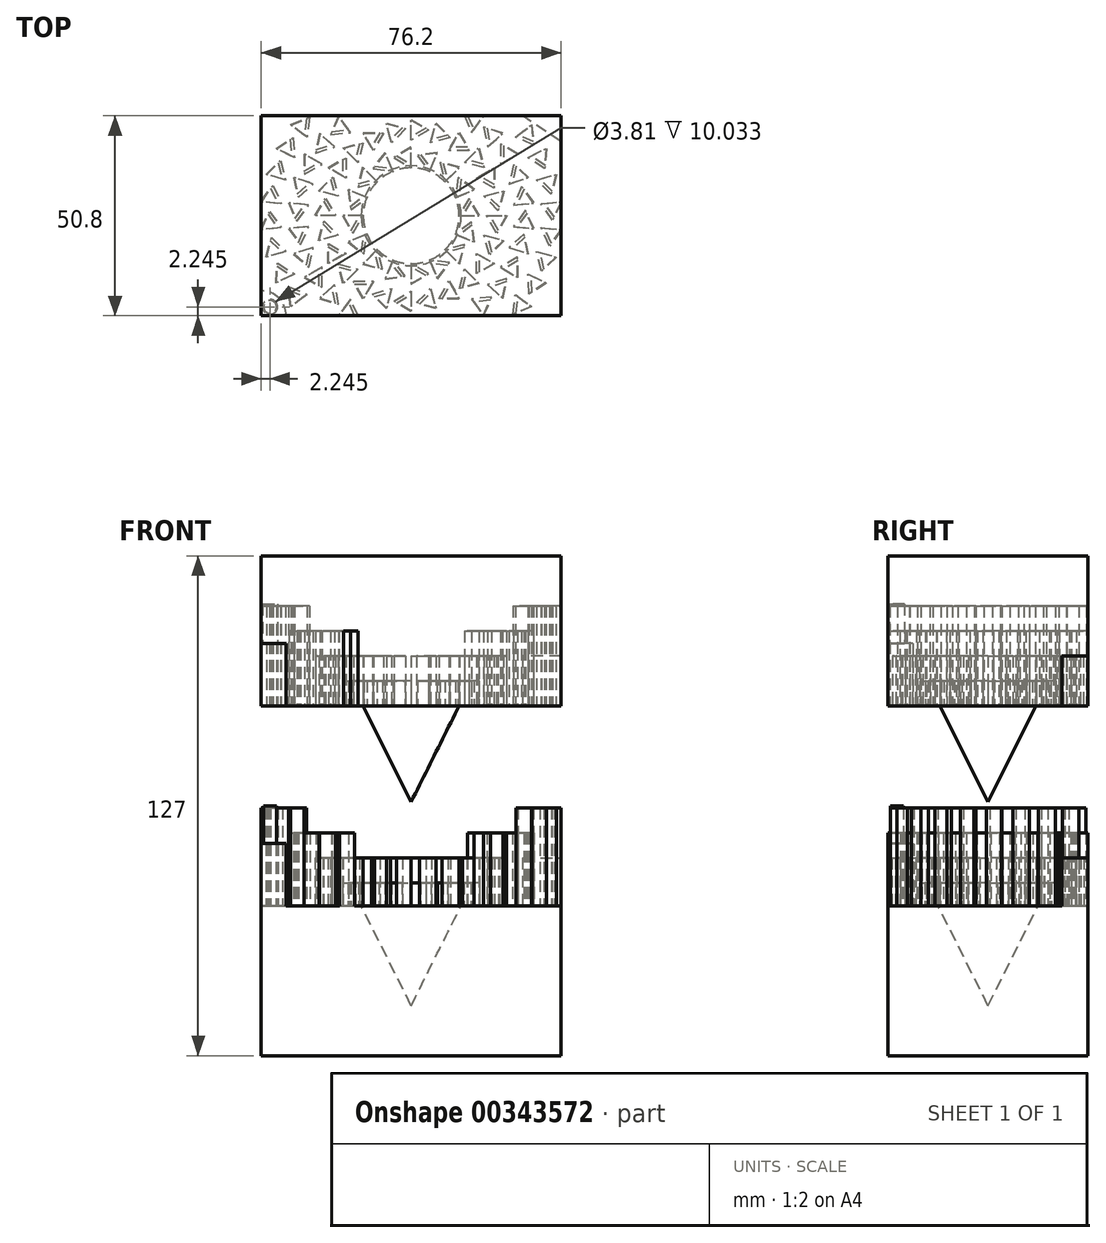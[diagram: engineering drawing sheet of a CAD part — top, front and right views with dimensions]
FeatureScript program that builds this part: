
annotation { "Feature Type Name" : "Feature", "Feature Type Description" : "" }
export const myFeature = defineFeature(function(context is Context, id is Id, definition is map)
    precondition{}
    {
        {
            var Q0;
            Q0=qCreatedBy(makeId("Top.planeOp"),FACE);
            var sketch = newSketch(context, id + "F0", { "sketchPlane" : qUnion([Q0])});
            skLineSegment(sketch, "E0.bottom", {"start": v(-38.1, 25.4) * mm, "end": v(38.1, 25.4) * mm});
            skLineSegment(sketch, "E0.top", {"start": v(-38.1, -25.4) * mm, "end": v(38.1, -25.4) * mm});
            skLineSegment(sketch, "E0.left", {"start": v(-38.1, 25.4) * mm, "end": v(-38.1, -25.4) * mm});
            skLineSegment(sketch, "E0.right", {"start": v(38.1, 25.4) * mm, "end": v(38.1, -25.4) * mm});
            skPoint(sketch, "E0.middle", {"position": v(0, 0) * mm});
            skSolve(sketch);
        }
        {
            var Q0;
            Q0=makeQuery(id+"F0.imprint","IMPRINT",FACE,{"disambiguationData":[TD([[makeQuery(id+"F0.imprint","IMPRINT",EDGE,{"derivedFrom":sQuery(id+"F0.wireOp",EDGE,"E0.bottom")}),-1.0]])]});
            extrude(context, id + "F1", {"entities" : qUnion([Q0]), "depth" : 38.1 * mm});
        }
        {
            var Q0;
            Q0=qCreatedBy(makeId("Top.planeOp"),FACE);
            cPlane(context, id + "F2", {"entities" : qUnion([Q0]), "cplaneType" : CPlaneType.OFFSET, "offset" : 127 * mm, "width" : 152.4 * mm, "height" : 152.4 * mm});
        }
        {
            var Q0;
            Q0=qCreatedBy(id+"F2.planeOp",FACE);
            var sketch = newSketch(context, id + "F3", { "sketchPlane" : qUnion([Q0])});
            skLineSegment(sketch, "E1.bottom", {"start": v(38.1, 25.4) * mm, "end": v(-38.1, 25.4) * mm});
            skLineSegment(sketch, "E1.top", {"start": v(38.1, -25.4) * mm, "end": v(-38.1, -25.4) * mm});
            skLineSegment(sketch, "E1.left", {"start": v(38.1, 25.4) * mm, "end": v(38.1, -25.4) * mm});
            skLineSegment(sketch, "E1.right", {"start": v(-38.1, 25.4) * mm, "end": v(-38.1, -25.4) * mm});
            skPoint(sketch, "E1.middle", {"position": v(0, 0) * mm});
            skSolve(sketch);
        }
        {
            var Q0;
            Q0=makeQuery(id+"F3.imprint","IMPRINT",FACE,{"disambiguationData":[TD([[makeQuery(id+"F3.imprint","IMPRINT",EDGE,{"derivedFrom":sQuery(id+"F3.wireOp",EDGE,"E1.bottom")}),1.0]])]});
            extrude(context, id + "F4", {"entities" : qUnion([Q0]), "oppositeDirection" : true, "depth" : 38.1 * mm});
        }
        {
            var Q0;
            Q0=makeQuery(id+"F4.opExtrude","CAP_FACE",FACE,{"disambiguationData":[OSD([sQuery(id+"F3.wireOp",EDGE,"E1.bottom"),sQuery(id+"F3.wireOp",EDGE,"E1.top"),sQuery(id+"F3.wireOp",EDGE,"E1.left"),sQuery(id+"F3.wireOp",EDGE,"E1.right")])],"isStart":false});
            var sketch = newSketch(context, id + "F5", { "sketchPlane" : qUnion([Q0])});
            skCircle(sketch, "E2", {"center": v(0, 0) * mm, "radius": 12.2 * mm});
            skSolve(sketch);
        }
        {
            var Q0;
            Q0=qCreatedBy(id+"F2.planeOp",FACE);
            cPlane(context, id + "F6", {"entities" : qUnion([Q0]), "cplaneType" : CPlaneType.OFFSET, "offset" : 62.48 * mm, "oppositeDirection" : true, "width" : 152.4 * mm, "height" : 152.4 * mm});
        }
        {
            var Q0;
            Q0=qCreatedBy(id+"F6.planeOp",FACE);
            var sketch = newSketch(context, id + "F7", { "sketchPlane" : qUnion([Q0])});
            skPoint(sketch, "E3", {"position": v(0, 0) * mm});
            skSolve(sketch);
        }
        {
            var Q1;
            Q1=makeQuery(id+"F5.imprint","IMPRINT",FACE,{"disambiguationData":[TD([[makeQuery(id+"F5.imprint","IMPRINT",EDGE,{"derivedFrom":sQuery(id+"F5.wireOp",EDGE,"E2")}),1.0]])]});
            var Q2;
            Q2=sQuery(id+"F7.wireOp",VERTEX,"E3");
            loft(context, id + "F8", {"operationType" : NewBodyOperationType.ADD, "sheetProfilesArray" : [{ "sheetProfileEntities" : qUnion([Q1]) }, { "sheetProfileEntities" : qUnion([Q2]) }]});
        }
        {
            var Q0;
            Q0=makeQuery(id+"F1.opExtrude","CAP_EDGE",EDGE,{"disambiguationData":[OSD([sQuery(id+"F0.wireOp",EDGE,"E0.bottom")])],"isStart":false});
            cPoint(context, id + "F9", {"entities" : qUnion([Q0]), "parameter" : 0.5});
        }
        {
            var Q0;
            Q0=makeQuery(id+"F1.opExtrude","CAP_EDGE",EDGE,{"disambiguationData":[OSD([sQuery(id+"F0.wireOp",EDGE,"E0.top")])],"isStart":false});
            cPoint(context, id + "F10", {"entities" : qUnion([Q0]), "parameter" : 0.5});
        }
        {
            var Q0;
            Q0=qCreatedBy(makeId("Origin.pointOp"),VERTEX);
            var Q1;
            Q1 = qCreatedBy(id + "F9" ,VERTEX);
            var Q2;
            Q2 = qCreatedBy(id + "F10" ,VERTEX);
            cPlane(context, id + "F11", {"entities" : qUnion([Q0, Q1, Q2]), "cplaneType" : CPlaneType.THREE_POINT, "offset" : 25.4 * mm, "width" : 152.4 * mm, "height" : 152.4 * mm});
        }
        {
            var Q0;
            Q0=makeQuery(id+"F4.opExtrude","CAP_FACE",FACE,{"disambiguationData":[OSD([sQuery(id+"F3.wireOp",EDGE,"E1.bottom"),sQuery(id+"F3.wireOp",EDGE,"E1.top"),sQuery(id+"F3.wireOp",EDGE,"E1.left"),sQuery(id+"F3.wireOp",EDGE,"E1.right")])],"isStart":false});
            var sketch = newSketch(context, id + "F12", { "sketchPlane" : qUnion([Q0])});
            skLineSegment(sketch, "E4", {"start": v(0, 12.2) * mm, "end": v(0, 17.27) * mm});
            skLineSegment(sketch, "E5", {"start": v(0, 17.27) * mm, "end": v(4.4, 14.73) * mm});
            skLineSegment(sketch, "E6", {"start": v(4.4, 14.73) * mm, "end": v(0, 12.2) * mm});
            skLineSegment(sketch, "E7.1.0", {"start": v(-6.6, 15.96) * mm, "end": v(-1.57, 15.3) * mm});
            skLineSegment(sketch, "E7.1.1", {"start": v(-1.57, 15.3) * mm, "end": v(-4.67, 11.26) * mm});
            skLineSegment(sketch, "E7.1.2", {"start": v(-4.67, 11.26) * mm, "end": v(-6.6, 15.96) * mm});
            skLineSegment(sketch, "E7.2.0", {"start": v(-12.21, 12.21) * mm, "end": v(-7.3, 13.53) * mm});
            skLineSegment(sketch, "E7.2.1", {"start": v(-7.3, 13.53) * mm, "end": v(-8.62, 8.62) * mm});
            skLineSegment(sketch, "E7.2.2", {"start": v(-8.62, 8.62) * mm, "end": v(-12.21, 12.21) * mm});
            skPoint(sketch, "E7.center", {"position": v(0, 0) * mm});
            skLineSegment(sketch, "E8.1.3.0", {"start": v(-15.96, 6.6) * mm, "end": v(-11.93, 9.7) * mm});
            skLineSegment(sketch, "E8.3.3.0", {"start": v(-11.93, 9.7) * mm, "end": v(-11.26, 4.67) * mm});
            skLineSegment(sketch, "E8.6.3.0", {"start": v(-11.26, 4.67) * mm, "end": v(-15.96, 6.6) * mm});
            skLineSegment(sketch, "E8.1.4.0", {"start": v(-17.27, 0) * mm, "end": v(-14.73, 4.4) * mm});
            skLineSegment(sketch, "E8.3.4.0", {"start": v(-14.73, 4.4) * mm, "end": v(-12.2, 0) * mm});
            skLineSegment(sketch, "E8.6.4.0", {"start": v(-12.2, 0) * mm, "end": v(-17.27, 0) * mm});
            skLineSegment(sketch, "E8.1.5.0", {"start": v(-15.96, -6.6) * mm, "end": v(-15.3, -1.57) * mm});
            skLineSegment(sketch, "E8.3.5.0", {"start": v(-15.3, -1.57) * mm, "end": v(-11.26, -4.67) * mm});
            skLineSegment(sketch, "E8.6.5.0", {"start": v(-11.26, -4.67) * mm, "end": v(-15.96, -6.6) * mm});
            skLineSegment(sketch, "E8.1.6.0", {"start": v(-12.21, -12.21) * mm, "end": v(-13.53, -7.3) * mm});
            skLineSegment(sketch, "E8.3.6.0", {"start": v(-13.53, -7.3) * mm, "end": v(-8.62, -8.62) * mm});
            skLineSegment(sketch, "E8.6.6.0", {"start": v(-8.62, -8.62) * mm, "end": v(-12.21, -12.21) * mm});
            skLineSegment(sketch, "E8.1.7.0", {"start": v(-6.6, -15.96) * mm, "end": v(-9.7, -11.93) * mm});
            skLineSegment(sketch, "E8.3.7.0", {"start": v(-9.7, -11.93) * mm, "end": v(-4.67, -11.26) * mm});
            skLineSegment(sketch, "E8.6.7.0", {"start": v(-4.67, -11.26) * mm, "end": v(-6.6, -15.96) * mm});
            skLineSegment(sketch, "E9.1.8.0", {"start": v(0, -17.27) * mm, "end": v(-4.4, -14.73) * mm});
            skLineSegment(sketch, "E9.3.8.0", {"start": v(-4.4, -14.73) * mm, "end": v(0, -12.2) * mm});
            skLineSegment(sketch, "E9.6.8.0", {"start": v(0, -12.2) * mm, "end": v(0, -17.27) * mm});
            skLineSegment(sketch, "E10.1.9.0", {"start": v(6.6, -15.96) * mm, "end": v(1.57, -15.3) * mm});
            skLineSegment(sketch, "E10.3.9.0", {"start": v(1.57, -15.3) * mm, "end": v(4.67, -11.26) * mm});
            skLineSegment(sketch, "E10.6.9.0", {"start": v(4.67, -11.26) * mm, "end": v(6.6, -15.96) * mm});
            skLineSegment(sketch, "E10.1.10.0", {"start": v(12.21, -12.21) * mm, "end": v(7.3, -13.53) * mm});
            skLineSegment(sketch, "E10.3.10.0", {"start": v(7.3, -13.53) * mm, "end": v(8.62, -8.62) * mm});
            skLineSegment(sketch, "E10.6.10.0", {"start": v(8.62, -8.62) * mm, "end": v(12.21, -12.21) * mm});
            skLineSegment(sketch, "E11.1.11.0", {"start": v(15.96, -6.6) * mm, "end": v(11.93, -9.7) * mm});
            skLineSegment(sketch, "E11.3.11.0", {"start": v(11.93, -9.7) * mm, "end": v(11.26, -4.67) * mm});
            skLineSegment(sketch, "E11.6.11.0", {"start": v(11.26, -4.67) * mm, "end": v(15.96, -6.6) * mm});
            skLineSegment(sketch, "E12.1.12.0", {"start": v(17.27, 0) * mm, "end": v(14.73, -4.4) * mm});
            skLineSegment(sketch, "E12.3.12.0", {"start": v(14.73, -4.4) * mm, "end": v(12.2, 0) * mm});
            skLineSegment(sketch, "E12.6.12.0", {"start": v(12.2, 0) * mm, "end": v(17.27, 0) * mm});
            skLineSegment(sketch, "E12.1.13.0", {"start": v(15.96, 6.6) * mm, "end": v(15.3, 1.57) * mm});
            skLineSegment(sketch, "E12.3.13.0", {"start": v(15.3, 1.57) * mm, "end": v(11.26, 4.67) * mm});
            skLineSegment(sketch, "E12.6.13.0", {"start": v(11.26, 4.67) * mm, "end": v(15.96, 6.6) * mm});
            skLineSegment(sketch, "E12.1.14.0", {"start": v(12.21, 12.21) * mm, "end": v(13.53, 7.3) * mm});
            skLineSegment(sketch, "E12.3.14.0", {"start": v(13.53, 7.3) * mm, "end": v(8.62, 8.62) * mm});
            skLineSegment(sketch, "E12.6.14.0", {"start": v(8.62, 8.62) * mm, "end": v(12.21, 12.21) * mm});
            skLineSegment(sketch, "E12.1.15.0", {"start": v(6.6, 15.96) * mm, "end": v(9.7, 11.93) * mm});
            skLineSegment(sketch, "E12.3.15.0", {"start": v(9.7, 11.93) * mm, "end": v(4.67, 11.26) * mm});
            skLineSegment(sketch, "E12.6.15.0", {"start": v(4.67, 11.26) * mm, "end": v(6.6, 15.96) * mm});
            skLineSegment(sketch, "E13", {"start": v(0, 19.18) * mm, "end": v(0, 24.26) * mm});
            skLineSegment(sketch, "E14", {"start": v(0, 24.26) * mm, "end": v(-4.4, 21.72) * mm});
            skLineSegment(sketch, "E15", {"start": v(-4.4, 21.72) * mm, "end": v(0, 19.18) * mm});
            skLineSegment(sketch, "E16.1.0", {"start": v(-6.28, 23.43) * mm, "end": v(-9.87, 19.84) * mm});
            skLineSegment(sketch, "E16.1.1", {"start": v(-4.96, 18.52) * mm, "end": v(-6.28, 23.43) * mm});
            skLineSegment(sketch, "E16.1.2", {"start": v(-9.87, 19.84) * mm, "end": v(-4.96, 18.52) * mm});
            skLineSegment(sketch, "E16.2.0", {"start": v(-12.13, 21) * mm, "end": v(-14.67, 16.6) * mm});
            skLineSegment(sketch, "E16.2.1", {"start": v(-9.59, 16.6) * mm, "end": v(-12.13, 21) * mm});
            skLineSegment(sketch, "E16.2.2", {"start": v(-14.67, 16.6) * mm, "end": v(-9.59, 16.6) * mm});
            skLineSegment(sketch, "E17.2.3.0", {"start": v(-17.15, 17.15) * mm, "end": v(-18.47, 12.25) * mm});
            skLineSegment(sketch, "E17.3.3.0", {"start": v(-13.56, 13.56) * mm, "end": v(-17.15, 17.15) * mm});
            skLineSegment(sketch, "E17.6.3.0", {"start": v(-18.47, 12.25) * mm, "end": v(-13.56, 13.56) * mm});
            skLineSegment(sketch, "E17.2.4.0", {"start": v(-21, 12.13) * mm, "end": v(-21, 7.05) * mm});
            skLineSegment(sketch, "E17.3.4.0", {"start": v(-16.6, 9.59) * mm, "end": v(-21, 12.13) * mm});
            skLineSegment(sketch, "E17.6.4.0", {"start": v(-21, 7.05) * mm, "end": v(-16.6, 9.59) * mm});
            skLineSegment(sketch, "E17.2.5.0", {"start": v(-23.43, 6.28) * mm, "end": v(-22.12, 1.37) * mm});
            skLineSegment(sketch, "E17.3.5.0", {"start": v(-18.52, 4.96) * mm, "end": v(-23.43, 6.28) * mm});
            skLineSegment(sketch, "E17.6.5.0", {"start": v(-22.12, 1.37) * mm, "end": v(-18.52, 4.96) * mm});
            skLineSegment(sketch, "E17.2.6.0", {"start": v(-24.26, 0) * mm, "end": v(-21.72, -4.4) * mm});
            skLineSegment(sketch, "E17.3.6.0", {"start": v(-19.18, 0) * mm, "end": v(-24.26, 0) * mm});
            skLineSegment(sketch, "E17.6.6.0", {"start": v(-21.72, -4.4) * mm, "end": v(-19.18, 0) * mm});
            skLineSegment(sketch, "E17.2.7.0", {"start": v(-23.43, -6.28) * mm, "end": v(-19.84, -9.87) * mm});
            skLineSegment(sketch, "E17.3.7.0", {"start": v(-18.52, -4.96) * mm, "end": v(-23.43, -6.28) * mm});
            skLineSegment(sketch, "E17.6.7.0", {"start": v(-19.84, -9.87) * mm, "end": v(-18.52, -4.96) * mm});
            skLineSegment(sketch, "E17.2.8.0", {"start": v(-21, -12.13) * mm, "end": v(-16.6, -14.67) * mm});
            skLineSegment(sketch, "E17.3.8.0", {"start": v(-16.6, -9.59) * mm, "end": v(-21, -12.13) * mm});
            skLineSegment(sketch, "E17.6.8.0", {"start": v(-16.6, -14.67) * mm, "end": v(-16.6, -9.59) * mm});
            skLineSegment(sketch, "E17.2.9.0", {"start": v(-17.15, -17.15) * mm, "end": v(-12.25, -18.47) * mm});
            skLineSegment(sketch, "E17.3.9.0", {"start": v(-13.56, -13.56) * mm, "end": v(-17.15, -17.15) * mm});
            skLineSegment(sketch, "E17.6.9.0", {"start": v(-12.25, -18.47) * mm, "end": v(-13.56, -13.56) * mm});
            skLineSegment(sketch, "E17.2.10.0", {"start": v(-12.13, -21) * mm, "end": v(-7.05, -21) * mm});
            skLineSegment(sketch, "E17.3.10.0", {"start": v(-9.59, -16.6) * mm, "end": v(-12.13, -21) * mm});
            skLineSegment(sketch, "E17.6.10.0", {"start": v(-7.05, -21) * mm, "end": v(-9.59, -16.6) * mm});
            skLineSegment(sketch, "E17.2.11.0", {"start": v(-6.28, -23.43) * mm, "end": v(-1.37, -22.12) * mm});
            skLineSegment(sketch, "E17.3.11.0", {"start": v(-4.96, -18.52) * mm, "end": v(-6.28, -23.43) * mm});
            skLineSegment(sketch, "E17.6.11.0", {"start": v(-1.37, -22.12) * mm, "end": v(-4.96, -18.52) * mm});
            skLineSegment(sketch, "E17.2.12.0", {"start": v(0, -24.26) * mm, "end": v(4.4, -21.72) * mm});
            skLineSegment(sketch, "E17.3.12.0", {"start": v(0, -19.18) * mm, "end": v(0, -24.26) * mm});
            skLineSegment(sketch, "E17.6.12.0", {"start": v(4.4, -21.72) * mm, "end": v(0, -19.18) * mm});
            skLineSegment(sketch, "E17.2.13.0", {"start": v(6.28, -23.43) * mm, "end": v(9.87, -19.84) * mm});
            skLineSegment(sketch, "E17.3.13.0", {"start": v(4.96, -18.52) * mm, "end": v(6.28, -23.43) * mm});
            skLineSegment(sketch, "E17.6.13.0", {"start": v(9.87, -19.84) * mm, "end": v(4.96, -18.52) * mm});
            skLineSegment(sketch, "E17.2.14.0", {"start": v(12.13, -21) * mm, "end": v(14.67, -16.6) * mm});
            skLineSegment(sketch, "E17.3.14.0", {"start": v(9.59, -16.6) * mm, "end": v(12.13, -21) * mm});
            skLineSegment(sketch, "E17.6.14.0", {"start": v(14.67, -16.6) * mm, "end": v(9.59, -16.6) * mm});
            skLineSegment(sketch, "E17.2.15.0", {"start": v(17.15, -17.15) * mm, "end": v(18.47, -12.25) * mm});
            skLineSegment(sketch, "E17.3.15.0", {"start": v(13.56, -13.56) * mm, "end": v(17.15, -17.15) * mm});
            skLineSegment(sketch, "E17.6.15.0", {"start": v(18.47, -12.25) * mm, "end": v(13.56, -13.56) * mm});
            skLineSegment(sketch, "E17.2.16.0", {"start": v(21, -12.13) * mm, "end": v(21, -7.05) * mm});
            skLineSegment(sketch, "E17.3.16.0", {"start": v(16.6, -9.59) * mm, "end": v(21, -12.13) * mm});
            skLineSegment(sketch, "E17.6.16.0", {"start": v(21, -7.05) * mm, "end": v(16.6, -9.59) * mm});
            skLineSegment(sketch, "E17.2.17.0", {"start": v(23.43, -6.28) * mm, "end": v(22.12, -1.37) * mm});
            skLineSegment(sketch, "E17.3.17.0", {"start": v(18.52, -4.96) * mm, "end": v(23.43, -6.28) * mm});
            skLineSegment(sketch, "E17.6.17.0", {"start": v(22.12, -1.37) * mm, "end": v(18.52, -4.96) * mm});
            skLineSegment(sketch, "E17.2.18.0", {"start": v(24.26, 0) * mm, "end": v(21.72, 4.4) * mm});
            skLineSegment(sketch, "E17.3.18.0", {"start": v(19.18, 0) * mm, "end": v(24.26, 0) * mm});
            skLineSegment(sketch, "E17.6.18.0", {"start": v(21.72, 4.4) * mm, "end": v(19.18, 0) * mm});
            skLineSegment(sketch, "E17.2.19.0", {"start": v(23.43, 6.28) * mm, "end": v(19.84, 9.87) * mm});
            skLineSegment(sketch, "E17.3.19.0", {"start": v(18.52, 4.96) * mm, "end": v(23.43, 6.28) * mm});
            skLineSegment(sketch, "E17.6.19.0", {"start": v(19.84, 9.87) * mm, "end": v(18.52, 4.96) * mm});
            skLineSegment(sketch, "E17.2.20.0", {"start": v(21, 12.13) * mm, "end": v(16.6, 14.67) * mm});
            skLineSegment(sketch, "E17.3.20.0", {"start": v(16.6, 9.59) * mm, "end": v(21, 12.13) * mm});
            skLineSegment(sketch, "E17.6.20.0", {"start": v(16.6, 14.67) * mm, "end": v(16.6, 9.59) * mm});
            skLineSegment(sketch, "E17.2.21.0", {"start": v(17.15, 17.15) * mm, "end": v(12.25, 18.47) * mm});
            skLineSegment(sketch, "E17.3.21.0", {"start": v(13.56, 13.56) * mm, "end": v(17.15, 17.15) * mm});
            skLineSegment(sketch, "E17.6.21.0", {"start": v(12.25, 18.47) * mm, "end": v(13.56, 13.56) * mm});
            skLineSegment(sketch, "E17.2.22.0", {"start": v(12.13, 21) * mm, "end": v(7.05, 21) * mm});
            skLineSegment(sketch, "E17.3.22.0", {"start": v(9.59, 16.6) * mm, "end": v(12.13, 21) * mm});
            skLineSegment(sketch, "E17.6.22.0", {"start": v(7.05, 21) * mm, "end": v(9.59, 16.6) * mm});
            skLineSegment(sketch, "E17.2.23.0", {"start": v(6.28, 23.43) * mm, "end": v(1.37, 22.12) * mm});
            skLineSegment(sketch, "E17.3.23.0", {"start": v(4.96, 18.52) * mm, "end": v(6.28, 23.43) * mm});
            skLineSegment(sketch, "E17.6.23.0", {"start": v(1.37, 22.12) * mm, "end": v(4.96, 18.52) * mm});
            skLineSegment(sketch, "E18", {"start": v(0, 26.16) * mm, "end": v(0, 31.24) * mm});
            skPoint(sketch, "E18.startSnap0", {"position": v(0, 25.4) * mm});
            skLineSegment(sketch, "E19", {"start": v(0, 31.24) * mm, "end": v(4.4, 28.7) * mm});
            skLineSegment(sketch, "E20", {"start": v(4.4, 28.7) * mm, "end": v(0, 26.16) * mm});
            skLineSegment(sketch, "E21.1.0", {"start": v(-5.44, 25.6) * mm, "end": v(-6.5, 30.56) * mm});
            skLineSegment(sketch, "E21.1.1", {"start": v(-6.5, 30.56) * mm, "end": v(-1.66, 28.99) * mm});
            skLineSegment(sketch, "E21.1.2", {"start": v(-1.66, 28.99) * mm, "end": v(-5.44, 25.6) * mm});
            skLineSegment(sketch, "E21.2.0", {"start": v(-10.64, 23.9) * mm, "end": v(-12.7, 28.54) * mm});
            skLineSegment(sketch, "E21.2.1", {"start": v(-12.7, 28.54) * mm, "end": v(-7.66, 28) * mm});
            skLineSegment(sketch, "E21.2.2", {"start": v(-7.66, 28) * mm, "end": v(-10.64, 23.9) * mm});
            skLineSegment(sketch, "E22.1.3.0", {"start": v(-15.38, 21.17) * mm, "end": v(-18.36, 25.28) * mm});
            skLineSegment(sketch, "E22.3.3.0", {"start": v(-18.36, 25.28) * mm, "end": v(-13.31, 25.8) * mm});
            skLineSegment(sketch, "E22.6.3.0", {"start": v(-13.31, 25.8) * mm, "end": v(-15.38, 21.17) * mm});
            skLineSegment(sketch, "E22.1.4.0", {"start": v(-19.44, 17.5) * mm, "end": v(-23.22, 20.9) * mm});
            skLineSegment(sketch, "E22.3.4.0", {"start": v(-23.22, 20.9) * mm, "end": v(-18.39, 22.47) * mm});
            skLineSegment(sketch, "E22.6.4.0", {"start": v(-18.39, 22.47) * mm, "end": v(-19.44, 17.5) * mm});
            skLineSegment(sketch, "E22.1.5.0", {"start": v(-22.66, 13.08) * mm, "end": v(-27.06, 15.62) * mm});
            skLineSegment(sketch, "E22.3.5.0", {"start": v(-27.06, 15.62) * mm, "end": v(-22.66, 18.16) * mm});
            skLineSegment(sketch, "E22.6.5.0", {"start": v(-22.66, 18.16) * mm, "end": v(-22.66, 13.08) * mm});
            skLineSegment(sketch, "E22.1.6.0", {"start": v(-24.88, 8.08) * mm, "end": v(-29.71, 9.65) * mm});
            skLineSegment(sketch, "E22.3.6.0", {"start": v(-29.71, 9.65) * mm, "end": v(-25.94, 13.05) * mm});
            skLineSegment(sketch, "E22.6.6.0", {"start": v(-25.94, 13.05) * mm, "end": v(-24.88, 8.08) * mm});
            skLineSegment(sketch, "E22.1.7.0", {"start": v(-26.02, 2.73) * mm, "end": v(-31.07, 3.27) * mm});
            skLineSegment(sketch, "E22.3.7.0", {"start": v(-31.07, 3.27) * mm, "end": v(-28.08, 7.38) * mm});
            skLineSegment(sketch, "E22.6.7.0", {"start": v(-28.08, 7.38) * mm, "end": v(-26.02, 2.73) * mm});
            skLineSegment(sketch, "E22.1.8.0", {"start": v(-26.02, -2.73) * mm, "end": v(-31.07, -3.27) * mm});
            skLineSegment(sketch, "E22.3.8.0", {"start": v(-31.07, -3.27) * mm, "end": v(-29, 1.38) * mm});
            skLineSegment(sketch, "E22.6.8.0", {"start": v(-29, 1.38) * mm, "end": v(-26.02, -2.73) * mm});
            skLineSegment(sketch, "E22.1.9.0", {"start": v(-24.88, -8.08) * mm, "end": v(-29.71, -9.65) * mm});
            skLineSegment(sketch, "E22.3.9.0", {"start": v(-29.71, -9.65) * mm, "end": v(-28.66, -4.69) * mm});
            skLineSegment(sketch, "E22.6.9.0", {"start": v(-28.66, -4.69) * mm, "end": v(-24.88, -8.08) * mm});
            skLineSegment(sketch, "E22.1.10.0", {"start": v(-22.66, -13.08) * mm, "end": v(-27.06, -15.62) * mm});
            skLineSegment(sketch, "E22.3.10.0", {"start": v(-27.06, -15.62) * mm, "end": v(-27.06, -10.54) * mm});
            skLineSegment(sketch, "E22.6.10.0", {"start": v(-27.06, -10.54) * mm, "end": v(-22.66, -13.08) * mm});
            skLineSegment(sketch, "E22.1.11.0", {"start": v(-19.44, -17.5) * mm, "end": v(-23.22, -20.9) * mm});
            skLineSegment(sketch, "E22.3.11.0", {"start": v(-23.22, -20.9) * mm, "end": v(-24.27, -15.94) * mm});
            skLineSegment(sketch, "E22.6.11.0", {"start": v(-24.27, -15.94) * mm, "end": v(-19.44, -17.5) * mm});
            skLineSegment(sketch, "E22.1.12.0", {"start": v(-15.38, -21.17) * mm, "end": v(-18.36, -25.28) * mm});
            skLineSegment(sketch, "E22.3.12.0", {"start": v(-18.36, -25.28) * mm, "end": v(-20.43, -20.63) * mm});
            skLineSegment(sketch, "E22.6.12.0", {"start": v(-20.43, -20.63) * mm, "end": v(-15.38, -21.17) * mm});
            skLineSegment(sketch, "E22.1.13.0", {"start": v(-10.64, -23.9) * mm, "end": v(-12.7, -28.54) * mm});
            skLineSegment(sketch, "E22.3.13.0", {"start": v(-12.7, -28.54) * mm, "end": v(-15.7, -24.43) * mm});
            skLineSegment(sketch, "E22.6.13.0", {"start": v(-15.7, -24.43) * mm, "end": v(-10.64, -23.9) * mm});
            skLineSegment(sketch, "E22.1.14.0", {"start": v(-5.44, -25.6) * mm, "end": v(-6.5, -30.56) * mm});
            skLineSegment(sketch, "E22.3.14.0", {"start": v(-6.5, -30.56) * mm, "end": v(-10.27, -27.16) * mm});
            skLineSegment(sketch, "E22.6.14.0", {"start": v(-10.27, -27.16) * mm, "end": v(-5.44, -25.6) * mm});
            skLineSegment(sketch, "E22.1.15.0", {"start": v(0, -26.16) * mm, "end": v(0, -31.24) * mm});
            skLineSegment(sketch, "E22.3.15.0", {"start": v(0, -31.24) * mm, "end": v(-4.4, -28.7) * mm});
            skLineSegment(sketch, "E22.6.15.0", {"start": v(-4.4, -28.7) * mm, "end": v(0, -26.16) * mm});
            skLineSegment(sketch, "E22.1.16.0", {"start": v(5.44, -25.6) * mm, "end": v(6.5, -30.56) * mm});
            skLineSegment(sketch, "E22.3.16.0", {"start": v(6.5, -30.56) * mm, "end": v(1.66, -28.99) * mm});
            skLineSegment(sketch, "E22.6.16.0", {"start": v(1.66, -28.99) * mm, "end": v(5.44, -25.6) * mm});
            skLineSegment(sketch, "E22.1.17.0", {"start": v(10.64, -23.9) * mm, "end": v(12.7, -28.54) * mm});
            skLineSegment(sketch, "E22.3.17.0", {"start": v(12.7, -28.54) * mm, "end": v(7.66, -28) * mm});
            skLineSegment(sketch, "E22.6.17.0", {"start": v(7.66, -28) * mm, "end": v(10.64, -23.9) * mm});
            skLineSegment(sketch, "E22.1.18.0", {"start": v(15.38, -21.17) * mm, "end": v(18.36, -25.28) * mm});
            skLineSegment(sketch, "E22.3.18.0", {"start": v(18.36, -25.28) * mm, "end": v(13.31, -25.8) * mm});
            skLineSegment(sketch, "E22.6.18.0", {"start": v(13.31, -25.8) * mm, "end": v(15.38, -21.17) * mm});
            skLineSegment(sketch, "E22.1.19.0", {"start": v(19.44, -17.5) * mm, "end": v(23.22, -20.9) * mm});
            skLineSegment(sketch, "E22.3.19.0", {"start": v(23.22, -20.9) * mm, "end": v(18.39, -22.47) * mm});
            skLineSegment(sketch, "E22.6.19.0", {"start": v(18.39, -22.47) * mm, "end": v(19.44, -17.5) * mm});
            skLineSegment(sketch, "E22.1.20.0", {"start": v(22.66, -13.08) * mm, "end": v(27.06, -15.62) * mm});
            skLineSegment(sketch, "E22.3.20.0", {"start": v(27.06, -15.62) * mm, "end": v(22.66, -18.16) * mm});
            skLineSegment(sketch, "E22.6.20.0", {"start": v(22.66, -18.16) * mm, "end": v(22.66, -13.08) * mm});
            skLineSegment(sketch, "E22.1.21.0", {"start": v(24.88, -8.08) * mm, "end": v(29.71, -9.65) * mm});
            skLineSegment(sketch, "E22.3.21.0", {"start": v(29.71, -9.65) * mm, "end": v(25.94, -13.05) * mm});
            skLineSegment(sketch, "E22.6.21.0", {"start": v(25.94, -13.05) * mm, "end": v(24.88, -8.08) * mm});
            skLineSegment(sketch, "E22.1.22.0", {"start": v(26.02, -2.73) * mm, "end": v(31.07, -3.27) * mm});
            skLineSegment(sketch, "E22.3.22.0", {"start": v(31.07, -3.27) * mm, "end": v(28.08, -7.38) * mm});
            skLineSegment(sketch, "E22.6.22.0", {"start": v(28.08, -7.38) * mm, "end": v(26.02, -2.73) * mm});
            skLineSegment(sketch, "E22.1.23.0", {"start": v(26.02, 2.73) * mm, "end": v(31.07, 3.27) * mm});
            skLineSegment(sketch, "E22.3.23.0", {"start": v(31.07, 3.27) * mm, "end": v(29, -1.38) * mm});
            skLineSegment(sketch, "E22.6.23.0", {"start": v(29, -1.38) * mm, "end": v(26.02, 2.73) * mm});
            skLineSegment(sketch, "E22.1.24.0", {"start": v(24.88, 8.08) * mm, "end": v(29.71, 9.65) * mm});
            skLineSegment(sketch, "E22.3.24.0", {"start": v(29.71, 9.65) * mm, "end": v(28.66, 4.69) * mm});
            skLineSegment(sketch, "E22.6.24.0", {"start": v(28.66, 4.69) * mm, "end": v(24.88, 8.08) * mm});
            skLineSegment(sketch, "E22.1.25.0", {"start": v(22.66, 13.08) * mm, "end": v(27.06, 15.62) * mm});
            skLineSegment(sketch, "E22.3.25.0", {"start": v(27.06, 15.62) * mm, "end": v(27.06, 10.54) * mm});
            skLineSegment(sketch, "E22.6.25.0", {"start": v(27.06, 10.54) * mm, "end": v(22.66, 13.08) * mm});
            skLineSegment(sketch, "E22.1.26.0", {"start": v(19.44, 17.5) * mm, "end": v(23.22, 20.9) * mm});
            skLineSegment(sketch, "E22.3.26.0", {"start": v(23.22, 20.9) * mm, "end": v(24.27, 15.94) * mm});
            skLineSegment(sketch, "E22.6.26.0", {"start": v(24.27, 15.94) * mm, "end": v(19.44, 17.5) * mm});
            skLineSegment(sketch, "E22.1.27.0", {"start": v(15.38, 21.17) * mm, "end": v(18.36, 25.28) * mm});
            skLineSegment(sketch, "E22.3.27.0", {"start": v(18.36, 25.28) * mm, "end": v(20.43, 20.63) * mm});
            skLineSegment(sketch, "E22.6.27.0", {"start": v(20.43, 20.63) * mm, "end": v(15.38, 21.17) * mm});
            skLineSegment(sketch, "E22.1.28.0", {"start": v(10.64, 23.9) * mm, "end": v(12.7, 28.54) * mm});
            skLineSegment(sketch, "E22.3.28.0", {"start": v(12.7, 28.54) * mm, "end": v(15.7, 24.43) * mm});
            skLineSegment(sketch, "E22.6.28.0", {"start": v(15.7, 24.43) * mm, "end": v(10.64, 23.9) * mm});
            skLineSegment(sketch, "E22.1.29.0", {"start": v(5.44, 25.6) * mm, "end": v(6.5, 30.56) * mm});
            skLineSegment(sketch, "E22.3.29.0", {"start": v(6.5, 30.56) * mm, "end": v(10.27, 27.16) * mm});
            skLineSegment(sketch, "E22.6.29.0", {"start": v(10.27, 27.16) * mm, "end": v(5.44, 25.6) * mm});
            skLineSegment(sketch, "E23", {"start": v(0, 33.15) * mm, "end": v(0, 38.23) * mm});
            skLineSegment(sketch, "E24", {"start": v(0, 38.23) * mm, "end": v(-4.4, 35.69) * mm});
            skLineSegment(sketch, "E25", {"start": v(-4.4, 35.69) * mm, "end": v(0, 33.15) * mm});
            skLineSegment(sketch, "E26.1.0", {"start": v(-6.1, 32.58) * mm, "end": v(-7.02, 37.58) * mm});
            skLineSegment(sketch, "E26.1.1", {"start": v(-7.02, 37.58) * mm, "end": v(-10.88, 34.27) * mm});
            skLineSegment(sketch, "E26.1.2", {"start": v(-10.88, 34.27) * mm, "end": v(-6.1, 32.58) * mm});
            skLineSegment(sketch, "E26.2.0", {"start": v(-11.97, 30.9) * mm, "end": v(-13.8, 35.65) * mm});
            skLineSegment(sketch, "E26.2.1", {"start": v(-13.8, 35.65) * mm, "end": v(-17, 31.69) * mm});
            skLineSegment(sketch, "E26.2.2", {"start": v(-17, 31.69) * mm, "end": v(-11.97, 30.9) * mm});
            skLineSegment(sketch, "E27.1.3.0", {"start": v(-17.45, 28.18) * mm, "end": v(-20.12, 32.5) * mm});
            skLineSegment(sketch, "E27.3.3.0", {"start": v(-20.12, 32.5) * mm, "end": v(-22.53, 28.03) * mm});
            skLineSegment(sketch, "E27.6.3.0", {"start": v(-22.53, 28.03) * mm, "end": v(-17.45, 28.18) * mm});
            skLineSegment(sketch, "E27.1.4.0", {"start": v(-22.33, 24.5) * mm, "end": v(-25.75, 28.25) * mm});
            skLineSegment(sketch, "E27.3.4.0", {"start": v(-25.75, 28.25) * mm, "end": v(-27.3, 23.4) * mm});
            skLineSegment(sketch, "E27.6.4.0", {"start": v(-27.3, 23.4) * mm, "end": v(-22.33, 24.5) * mm});
            skLineSegment(sketch, "E27.1.5.0", {"start": v(-26.45, 19.98) * mm, "end": v(-30.5, 23.04) * mm});
            skLineSegment(sketch, "E27.3.5.0", {"start": v(-30.5, 23.04) * mm, "end": v(-31.13, 18) * mm});
            skLineSegment(sketch, "E27.6.5.0", {"start": v(-31.13, 18) * mm, "end": v(-26.45, 19.98) * mm});
            skLineSegment(sketch, "E27.1.6.0", {"start": v(-29.67, 14.77) * mm, "end": v(-34.22, 17.04) * mm});
            skLineSegment(sketch, "E27.3.6.0", {"start": v(-34.22, 17.04) * mm, "end": v(-33.9, 11.97) * mm});
            skLineSegment(sketch, "E27.6.6.0", {"start": v(-33.9, 11.97) * mm, "end": v(-29.67, 14.77) * mm});
            skLineSegment(sketch, "E27.1.7.0", {"start": v(-31.88, 9.07) * mm, "end": v(-36.77, 10.46) * mm});
            skLineSegment(sketch, "E27.3.7.0", {"start": v(-36.77, 10.46) * mm, "end": v(-35.53, 5.53) * mm});
            skLineSegment(sketch, "E27.6.7.0", {"start": v(-35.53, 5.53) * mm, "end": v(-31.88, 9.07) * mm});
            skLineSegment(sketch, "E27.1.8.0", {"start": v(-33, 3.06) * mm, "end": v(-38.06, 3.53) * mm});
            skLineSegment(sketch, "E27.3.8.0", {"start": v(-38.06, 3.53) * mm, "end": v(-35.94, -1.09) * mm});
            skLineSegment(sketch, "E27.6.8.0", {"start": v(-35.94, -1.09) * mm, "end": v(-33, 3.06) * mm});
            skLineSegment(sketch, "E27.1.9.0", {"start": v(-33, -3.06) * mm, "end": v(-38.06, -3.53) * mm});
            skLineSegment(sketch, "E27.3.9.0", {"start": v(-38.06, -3.53) * mm, "end": v(-35.13, -7.67) * mm});
            skLineSegment(sketch, "E27.6.9.0", {"start": v(-35.13, -7.67) * mm, "end": v(-33, -3.06) * mm});
            skLineSegment(sketch, "E27.1.10.0", {"start": v(-31.88, -9.07) * mm, "end": v(-36.77, -10.46) * mm});
            skLineSegment(sketch, "E27.3.10.0", {"start": v(-36.77, -10.46) * mm, "end": v(-33.12, -14) * mm});
            skLineSegment(sketch, "E27.6.10.0", {"start": v(-33.12, -14) * mm, "end": v(-31.88, -9.07) * mm});
            skLineSegment(sketch, "E27.1.11.0", {"start": v(-29.67, -14.77) * mm, "end": v(-34.22, -17.04) * mm});
            skLineSegment(sketch, "E27.3.11.0", {"start": v(-34.22, -17.04) * mm, "end": v(-29.98, -19.85) * mm});
            skLineSegment(sketch, "E27.6.11.0", {"start": v(-29.98, -19.85) * mm, "end": v(-29.67, -14.77) * mm});
            skLineSegment(sketch, "E27.1.12.0", {"start": v(-26.45, -19.98) * mm, "end": v(-30.5, -23.04) * mm});
            skLineSegment(sketch, "E27.3.12.0", {"start": v(-30.5, -23.04) * mm, "end": v(-25.83, -25.02) * mm});
            skLineSegment(sketch, "E27.6.12.0", {"start": v(-25.83, -25.02) * mm, "end": v(-26.45, -19.98) * mm});
            skLineSegment(sketch, "E27.1.13.0", {"start": v(-22.33, -24.5) * mm, "end": v(-25.75, -28.25) * mm});
            skLineSegment(sketch, "E27.3.13.0", {"start": v(-25.75, -28.25) * mm, "end": v(-20.8, -29.34) * mm});
            skLineSegment(sketch, "E27.6.13.0", {"start": v(-20.8, -29.34) * mm, "end": v(-22.33, -24.5) * mm});
            skLineSegment(sketch, "E27.1.14.0", {"start": v(-17.45, -28.18) * mm, "end": v(-20.12, -32.5) * mm});
            skLineSegment(sketch, "E27.3.14.0", {"start": v(-20.12, -32.5) * mm, "end": v(-15.05, -32.66) * mm});
            skLineSegment(sketch, "E27.6.14.0", {"start": v(-15.05, -32.66) * mm, "end": v(-17.45, -28.18) * mm});
            skLineSegment(sketch, "E27.1.15.0", {"start": v(-11.97, -30.9) * mm, "end": v(-13.8, -35.65) * mm});
            skLineSegment(sketch, "E27.3.15.0", {"start": v(-13.8, -35.65) * mm, "end": v(-8.79, -34.87) * mm});
            skLineSegment(sketch, "E27.6.15.0", {"start": v(-8.79, -34.87) * mm, "end": v(-11.97, -30.9) * mm});
            skLineSegment(sketch, "E27.1.16.0", {"start": v(-6.1, -32.58) * mm, "end": v(-7.02, -37.58) * mm});
            skLineSegment(sketch, "E27.3.16.0", {"start": v(-7.02, -37.58) * mm, "end": v(-2.23, -35.89) * mm});
            skLineSegment(sketch, "E27.6.16.0", {"start": v(-2.23, -35.89) * mm, "end": v(-6.1, -32.58) * mm});
            skLineSegment(sketch, "E27.1.17.0", {"start": v(0, -33.15) * mm, "end": v(0, -38.23) * mm});
            skLineSegment(sketch, "E27.3.17.0", {"start": v(0, -38.23) * mm, "end": v(4.4, -35.69) * mm});
            skLineSegment(sketch, "E27.6.17.0", {"start": v(4.4, -35.69) * mm, "end": v(0, -33.15) * mm});
            skLineSegment(sketch, "E27.1.18.0", {"start": v(6.1, -32.58) * mm, "end": v(7.02, -37.58) * mm});
            skLineSegment(sketch, "E27.3.18.0", {"start": v(7.02, -37.58) * mm, "end": v(10.88, -34.27) * mm});
            skLineSegment(sketch, "E27.6.18.0", {"start": v(10.88, -34.27) * mm, "end": v(6.1, -32.58) * mm});
            skLineSegment(sketch, "E27.1.19.0", {"start": v(11.97, -30.9) * mm, "end": v(13.8, -35.65) * mm});
            skLineSegment(sketch, "E27.3.19.0", {"start": v(13.8, -35.65) * mm, "end": v(17, -31.69) * mm});
            skLineSegment(sketch, "E27.6.19.0", {"start": v(17, -31.69) * mm, "end": v(11.97, -30.9) * mm});
            skLineSegment(sketch, "E27.1.20.0", {"start": v(17.45, -28.18) * mm, "end": v(20.12, -32.5) * mm});
            skLineSegment(sketch, "E27.3.20.0", {"start": v(20.12, -32.5) * mm, "end": v(22.53, -28.03) * mm});
            skLineSegment(sketch, "E27.6.20.0", {"start": v(22.53, -28.03) * mm, "end": v(17.45, -28.18) * mm});
            skLineSegment(sketch, "E27.1.21.0", {"start": v(22.33, -24.5) * mm, "end": v(25.75, -28.25) * mm});
            skLineSegment(sketch, "E27.3.21.0", {"start": v(25.75, -28.25) * mm, "end": v(27.3, -23.4) * mm});
            skLineSegment(sketch, "E27.6.21.0", {"start": v(27.3, -23.4) * mm, "end": v(22.33, -24.5) * mm});
            skLineSegment(sketch, "E27.1.22.0", {"start": v(26.45, -19.98) * mm, "end": v(30.5, -23.04) * mm});
            skLineSegment(sketch, "E27.3.22.0", {"start": v(30.5, -23.04) * mm, "end": v(31.13, -18) * mm});
            skLineSegment(sketch, "E27.6.22.0", {"start": v(31.13, -18) * mm, "end": v(26.45, -19.98) * mm});
            skLineSegment(sketch, "E27.1.23.0", {"start": v(29.67, -14.77) * mm, "end": v(34.22, -17.04) * mm});
            skLineSegment(sketch, "E27.3.23.0", {"start": v(34.22, -17.04) * mm, "end": v(33.9, -11.97) * mm});
            skLineSegment(sketch, "E27.6.23.0", {"start": v(33.9, -11.97) * mm, "end": v(29.67, -14.77) * mm});
            skLineSegment(sketch, "E27.1.24.0", {"start": v(31.88, -9.07) * mm, "end": v(36.77, -10.46) * mm});
            skLineSegment(sketch, "E27.3.24.0", {"start": v(36.77, -10.46) * mm, "end": v(35.53, -5.53) * mm});
            skLineSegment(sketch, "E27.6.24.0", {"start": v(35.53, -5.53) * mm, "end": v(31.88, -9.07) * mm});
            skLineSegment(sketch, "E27.1.25.0", {"start": v(33, -3.06) * mm, "end": v(38.06, -3.53) * mm});
            skLineSegment(sketch, "E27.3.25.0", {"start": v(38.06, -3.53) * mm, "end": v(35.94, 1.09) * mm});
            skLineSegment(sketch, "E27.6.25.0", {"start": v(35.94, 1.09) * mm, "end": v(33, -3.06) * mm});
            skLineSegment(sketch, "E27.1.26.0", {"start": v(33, 3.06) * mm, "end": v(38.06, 3.53) * mm});
            skLineSegment(sketch, "E27.3.26.0", {"start": v(38.06, 3.53) * mm, "end": v(35.13, 7.67) * mm});
            skLineSegment(sketch, "E27.6.26.0", {"start": v(35.13, 7.67) * mm, "end": v(33, 3.06) * mm});
            skLineSegment(sketch, "E27.1.27.0", {"start": v(31.88, 9.07) * mm, "end": v(36.77, 10.46) * mm});
            skLineSegment(sketch, "E27.3.27.0", {"start": v(36.77, 10.46) * mm, "end": v(33.12, 14) * mm});
            skLineSegment(sketch, "E27.6.27.0", {"start": v(33.12, 14) * mm, "end": v(31.88, 9.07) * mm});
            skLineSegment(sketch, "E27.1.28.0", {"start": v(29.67, 14.77) * mm, "end": v(34.22, 17.04) * mm});
            skLineSegment(sketch, "E27.3.28.0", {"start": v(34.22, 17.04) * mm, "end": v(29.98, 19.85) * mm});
            skLineSegment(sketch, "E27.6.28.0", {"start": v(29.98, 19.85) * mm, "end": v(29.67, 14.77) * mm});
            skLineSegment(sketch, "E27.1.29.0", {"start": v(26.45, 19.98) * mm, "end": v(30.5, 23.04) * mm});
            skLineSegment(sketch, "E27.3.29.0", {"start": v(30.5, 23.04) * mm, "end": v(25.83, 25.02) * mm});
            skLineSegment(sketch, "E27.6.29.0", {"start": v(25.83, 25.02) * mm, "end": v(26.45, 19.98) * mm});
            skLineSegment(sketch, "E27.1.30.0", {"start": v(22.33, 24.5) * mm, "end": v(25.75, 28.25) * mm});
            skLineSegment(sketch, "E27.3.30.0", {"start": v(25.75, 28.25) * mm, "end": v(20.8, 29.34) * mm});
            skLineSegment(sketch, "E27.6.30.0", {"start": v(20.8, 29.34) * mm, "end": v(22.33, 24.5) * mm});
            skLineSegment(sketch, "E27.1.31.0", {"start": v(17.45, 28.18) * mm, "end": v(20.12, 32.5) * mm});
            skLineSegment(sketch, "E27.3.31.0", {"start": v(20.12, 32.5) * mm, "end": v(15.05, 32.66) * mm});
            skLineSegment(sketch, "E27.6.31.0", {"start": v(15.05, 32.66) * mm, "end": v(17.45, 28.18) * mm});
            skLineSegment(sketch, "E27.1.32.0", {"start": v(11.97, 30.9) * mm, "end": v(13.8, 35.65) * mm});
            skLineSegment(sketch, "E27.3.32.0", {"start": v(13.8, 35.65) * mm, "end": v(8.79, 34.87) * mm});
            skLineSegment(sketch, "E27.6.32.0", {"start": v(8.79, 34.87) * mm, "end": v(11.97, 30.9) * mm});
            skLineSegment(sketch, "E27.1.33.0", {"start": v(6.1, 32.58) * mm, "end": v(7.02, 37.58) * mm});
            skLineSegment(sketch, "E27.3.33.0", {"start": v(7.02, 37.58) * mm, "end": v(2.23, 35.89) * mm});
            skLineSegment(sketch, "E27.6.33.0", {"start": v(2.23, 35.89) * mm, "end": v(6.1, 32.58) * mm});
            skSolve(sketch);
        }
        {
            var Q0;
            Q0=makeQuery(id+"F12.imprint","IMPRINT",FACE,{"disambiguationData":[TD([[makeQuery(id+"F12.imprint","IMPRINT",EDGE,{"derivedFrom":sQuery(id+"F12.wireOp",EDGE,"E4")}),-1.0]])]});
            var Q1;
            Q1=makeQuery(id+"F12.imprint","IMPRINT",FACE,{"disambiguationData":[TD([[makeQuery(id+"F12.imprint","IMPRINT",EDGE,{"derivedFrom":sQuery(id+"F12.wireOp",EDGE,"E7.1.0")}),-1.0]])]});
            var Q2;
            Q2=makeQuery(id+"F12.imprint","IMPRINT",FACE,{"disambiguationData":[TD([[makeQuery(id+"F12.imprint","IMPRINT",EDGE,{"derivedFrom":sQuery(id+"F12.wireOp",EDGE,"E7.2.0")}),-1.0]])]});
            var Q3;
            Q3=makeQuery(id+"F12.imprint","IMPRINT",FACE,{"disambiguationData":[TD([[makeQuery(id+"F12.imprint","IMPRINT",EDGE,{"derivedFrom":sQuery(id+"F12.wireOp",EDGE,"E8.1.3.0")}),-1.0]])]});
            var Q4;
            Q4=makeQuery(id+"F12.imprint","IMPRINT",FACE,{"disambiguationData":[TD([[makeQuery(id+"F12.imprint","IMPRINT",EDGE,{"derivedFrom":sQuery(id+"F12.wireOp",EDGE,"E8.1.4.0")}),-1.0]])]});
            var Q5;
            Q5=makeQuery(id+"F12.imprint","IMPRINT",FACE,{"disambiguationData":[TD([[makeQuery(id+"F12.imprint","IMPRINT",EDGE,{"derivedFrom":sQuery(id+"F12.wireOp",EDGE,"E8.1.5.0")}),-1.0]])]});
            var Q6;
            Q6=makeQuery(id+"F12.imprint","IMPRINT",FACE,{"disambiguationData":[TD([[makeQuery(id+"F12.imprint","IMPRINT",EDGE,{"derivedFrom":sQuery(id+"F12.wireOp",EDGE,"E8.1.6.0")}),-1.0]])]});
            var Q7;
            Q7=makeQuery(id+"F12.imprint","IMPRINT",FACE,{"disambiguationData":[TD([[makeQuery(id+"F12.imprint","IMPRINT",EDGE,{"derivedFrom":sQuery(id+"F12.wireOp",EDGE,"E8.1.7.0")}),-1.0]])]});
            var Q8;
            Q8=makeQuery(id+"F12.imprint","IMPRINT",FACE,{"disambiguationData":[TD([[makeQuery(id+"F12.imprint","IMPRINT",EDGE,{"derivedFrom":sQuery(id+"F12.wireOp",EDGE,"E9.1.8.0")}),-1.0]])]});
            var Q9;
            Q9=makeQuery(id+"F12.imprint","IMPRINT",FACE,{"disambiguationData":[TD([[makeQuery(id+"F12.imprint","IMPRINT",EDGE,{"derivedFrom":sQuery(id+"F12.wireOp",EDGE,"E10.1.9.0")}),-1.0]])]});
            var Q10;
            Q10=makeQuery(id+"F12.imprint","IMPRINT",FACE,{"disambiguationData":[TD([[makeQuery(id+"F12.imprint","IMPRINT",EDGE,{"derivedFrom":sQuery(id+"F12.wireOp",EDGE,"E10.1.10.0")}),-1.0]])]});
            var Q11;
            Q11=makeQuery(id+"F12.imprint","IMPRINT",FACE,{"disambiguationData":[TD([[makeQuery(id+"F12.imprint","IMPRINT",EDGE,{"derivedFrom":sQuery(id+"F12.wireOp",EDGE,"E11.1.11.0")}),-1.0]])]});
            var Q12;
            Q12=makeQuery(id+"F12.imprint","IMPRINT",FACE,{"disambiguationData":[TD([[makeQuery(id+"F12.imprint","IMPRINT",EDGE,{"derivedFrom":sQuery(id+"F12.wireOp",EDGE,"E12.1.18.0")}),-1.0]])]});
            var Q13;
            Q13=makeQuery(id+"F12.imprint","IMPRINT",FACE,{"disambiguationData":[TD([[makeQuery(id+"F12.imprint","IMPRINT",EDGE,{"derivedFrom":sQuery(id+"F12.wireOp",EDGE,"E12.1.19.0")}),-1.0]])]});
            var Q14;
            Q14=makeQuery(id+"F12.imprint","IMPRINT",FACE,{"disambiguationData":[TD([[makeQuery(id+"F12.imprint","IMPRINT",EDGE,{"derivedFrom":sQuery(id+"F12.wireOp",EDGE,"E12.1.17.0")}),-1.0]])]});
            var Q15;
            Q15=makeQuery(id+"F12.imprint","IMPRINT",FACE,{"disambiguationData":[TD([[makeQuery(id+"F12.imprint","IMPRINT",EDGE,{"derivedFrom":sQuery(id+"F12.wireOp",EDGE,"E12.1.13.0")}),-1.0]])]});
            var Q16;
            Q16=makeQuery(id+"F12.imprint","IMPRINT",FACE,{"disambiguationData":[TD([[makeQuery(id+"F12.imprint","IMPRINT",EDGE,{"derivedFrom":sQuery(id+"F12.wireOp",EDGE,"E12.1.12.0")}),-1.0]])]});
            var Q17;
            Q17=makeQuery(id+"F12.imprint","IMPRINT",FACE,{"disambiguationData":[TD([[makeQuery(id+"F12.imprint","IMPRINT",EDGE,{"derivedFrom":sQuery(id+"F12.wireOp",EDGE,"E12.1.14.0")}),-1.0]])]});
            var Q18;
            Q18=makeQuery(id+"F12.imprint","IMPRINT",FACE,{"disambiguationData":[TD([[makeQuery(id+"F12.imprint","IMPRINT",EDGE,{"derivedFrom":sQuery(id+"F12.wireOp",EDGE,"E12.1.15.0")}),-1.0]])]});
            var Q19;
            Q19=makeQuery(id+"F12.imprint","IMPRINT",FACE,{"disambiguationData":[TD([[makeQuery(id+"F12.imprint","IMPRINT",EDGE,{"derivedFrom":sQuery(id+"F12.wireOp",EDGE,"E12.1.16.0")}),-1.0]])]});
            extrude(context, id + "F13", {"entities" : qUnion([Q0, Q1, Q2, Q3, Q4, Q5, Q6, Q7, Q8, Q9, Q10, Q11, Q12, Q13, Q14, Q15, Q16, Q17, Q18, Q19]), "operationType" : NewBodyOperationType.REMOVE, "oppositeDirection" : true, "depth" : 6.35 * mm});
        }
        {
            var Q0;
            Q0=qCreatedBy(id+"F11.planeOp",FACE);
            var sketch = newSketch(context, id + "F14", { "sketchPlane" : qUnion([Q0])});
            skLineSegment(sketch, "E28", {"start": v(0, 38.07) * mm, "end": v(0, 38.1) * mm});
            skLineSegment(sketch, "E29", {"start": v(0, 38.1) * mm, "end": v(0, 12.7) * mm});
            skLineSegment(sketch, "E30", {"start": v(0, 38.1) * mm, "end": v(-12.7, 38.1) * mm});
            skLineSegment(sketch, "E31", {"start": v(0, 38.1) * mm, "end": v(12.7, 38.1) * mm});
            skLineSegment(sketch, "E32", {"start": v(0, 12.7) * mm, "end": v(-12.7, 38.1) * mm});
            skSolve(sketch);
        }
        {
            var Q0;
            {var subQ0=sQuery(id+"F14.wireOp",EDGE,"E30");Q0=makeQuery(id+"F14.imprint","IMPRINT",FACE,{"disambiguationData":[TD([[makeQuery(id+"F14.imprint","IMPRINT",EDGE,{"derivedFrom":subQ0}),1.0]])]});}
            var Q1;
            Q1=sQuery(id+"F14.wireOp",EDGE,"E29");
            revolve(context, id + "F15", {"operationType" : NewBodyOperationType.REMOVE, "entities" : qUnion([Q0]), "axis" : qUnion([Q1]), "revolveType" : RevolveType.FULL, "oppositeDirection" : true});
        }
        {
            var Q0;
            Q0=makeQuery(id+"F12.imprint","IMPRINT",FACE,{"disambiguationData":[TD([[makeQuery(id+"F12.imprint","IMPRINT",EDGE,{"derivedFrom":sQuery(id+"F12.wireOp",EDGE,"E16.1.0")}),1.0]])]});
            var Q1;
            Q1=makeQuery(id+"F12.imprint","IMPRINT",FACE,{"disambiguationData":[TD([[makeQuery(id+"F12.imprint","IMPRINT",EDGE,{"derivedFrom":sQuery(id+"F12.wireOp",EDGE,"E16.2.0")}),1.0]])]});
            var Q2;
            Q2=makeQuery(id+"F12.imprint","IMPRINT",FACE,{"disambiguationData":[TD([[makeQuery(id+"F12.imprint","IMPRINT",EDGE,{"derivedFrom":sQuery(id+"F12.wireOp",EDGE,"E17.2.3.0")}),1.0]])]});
            var Q3;
            Q3=makeQuery(id+"F12.imprint","IMPRINT",FACE,{"disambiguationData":[TD([[makeQuery(id+"F12.imprint","IMPRINT",EDGE,{"derivedFrom":sQuery(id+"F12.wireOp",EDGE,"E17.2.4.0")}),1.0]])]});
            var Q4;
            Q4=makeQuery(id+"F12.imprint","IMPRINT",FACE,{"disambiguationData":[TD([[makeQuery(id+"F12.imprint","IMPRINT",EDGE,{"derivedFrom":sQuery(id+"F12.wireOp",EDGE,"E17.2.5.0")}),1.0]])]});
            var Q5;
            Q5=makeQuery(id+"F12.imprint","IMPRINT",FACE,{"disambiguationData":[TD([[makeQuery(id+"F12.imprint","IMPRINT",EDGE,{"derivedFrom":sQuery(id+"F12.wireOp",EDGE,"E17.2.6.0")}),1.0]])]});
            var Q6;
            Q6=makeQuery(id+"F12.imprint","IMPRINT",FACE,{"disambiguationData":[TD([[makeQuery(id+"F12.imprint","IMPRINT",EDGE,{"derivedFrom":sQuery(id+"F12.wireOp",EDGE,"E17.2.7.0")}),1.0]])]});
            var Q7;
            Q7=makeQuery(id+"F12.imprint","IMPRINT",FACE,{"disambiguationData":[TD([[makeQuery(id+"F12.imprint","IMPRINT",EDGE,{"derivedFrom":sQuery(id+"F12.wireOp",EDGE,"E17.2.8.0")}),1.0]])]});
            var Q8;
            Q8=makeQuery(id+"F12.imprint","IMPRINT",FACE,{"disambiguationData":[TD([[makeQuery(id+"F12.imprint","IMPRINT",EDGE,{"derivedFrom":sQuery(id+"F12.wireOp",EDGE,"E17.2.9.0")}),1.0]])]});
            var Q9;
            Q9=makeQuery(id+"F12.imprint","IMPRINT",FACE,{"disambiguationData":[TD([[makeQuery(id+"F12.imprint","IMPRINT",EDGE,{"derivedFrom":sQuery(id+"F12.wireOp",EDGE,"E17.2.10.0")}),1.0]])]});
            var Q10;
            Q10=makeQuery(id+"F12.imprint","IMPRINT",FACE,{"disambiguationData":[TD([[makeQuery(id+"F12.imprint","IMPRINT",EDGE,{"derivedFrom":sQuery(id+"F12.wireOp",EDGE,"E17.2.11.0")}),1.0]])]});
            var Q11;
            Q11=makeQuery(id+"F12.imprint","IMPRINT",FACE,{"disambiguationData":[TD([[makeQuery(id+"F12.imprint","IMPRINT",EDGE,{"derivedFrom":sQuery(id+"F12.wireOp",EDGE,"E17.2.12.0")}),1.0]])]});
            var Q12;
            Q12=makeQuery(id+"F12.imprint","IMPRINT",FACE,{"disambiguationData":[TD([[makeQuery(id+"F12.imprint","IMPRINT",EDGE,{"derivedFrom":sQuery(id+"F12.wireOp",EDGE,"E17.2.13.0")}),1.0]])]});
            var Q13;
            Q13=makeQuery(id+"F12.imprint","IMPRINT",FACE,{"disambiguationData":[TD([[makeQuery(id+"F12.imprint","IMPRINT",EDGE,{"derivedFrom":sQuery(id+"F12.wireOp",EDGE,"E17.2.14.0")}),1.0]])]});
            var Q14;
            Q14=makeQuery(id+"F12.imprint","IMPRINT",FACE,{"disambiguationData":[TD([[makeQuery(id+"F12.imprint","IMPRINT",EDGE,{"derivedFrom":sQuery(id+"F12.wireOp",EDGE,"E17.2.15.0")}),1.0]])]});
            var Q15;
            Q15=makeQuery(id+"F12.imprint","IMPRINT",FACE,{"disambiguationData":[TD([[makeQuery(id+"F12.imprint","IMPRINT",EDGE,{"derivedFrom":sQuery(id+"F12.wireOp",EDGE,"E17.2.16.0")}),1.0]])]});
            var Q16;
            Q16=makeQuery(id+"F12.imprint","IMPRINT",FACE,{"disambiguationData":[TD([[makeQuery(id+"F12.imprint","IMPRINT",EDGE,{"derivedFrom":sQuery(id+"F12.wireOp",EDGE,"E17.2.23.0")}),1.0]])]});
            var Q17;
            Q17=makeQuery(id+"F12.imprint","IMPRINT",FACE,{"disambiguationData":[TD([[makeQuery(id+"F12.imprint","IMPRINT",EDGE,{"derivedFrom":sQuery(id+"F12.wireOp",EDGE,"E17.2.22.0")}),1.0]])]});
            var Q18;
            Q18=makeQuery(id+"F12.imprint","IMPRINT",FACE,{"disambiguationData":[TD([[makeQuery(id+"F12.imprint","IMPRINT",EDGE,{"derivedFrom":sQuery(id+"F12.wireOp",EDGE,"E17.2.21.0")}),1.0]])]});
            var Q19;
            Q19=makeQuery(id+"F12.imprint","IMPRINT",FACE,{"disambiguationData":[TD([[makeQuery(id+"F12.imprint","IMPRINT",EDGE,{"derivedFrom":sQuery(id+"F12.wireOp",EDGE,"E17.2.20.0")}),1.0]])]});
            var Q20;
            Q20=makeQuery(id+"F12.imprint","IMPRINT",FACE,{"disambiguationData":[TD([[makeQuery(id+"F12.imprint","IMPRINT",EDGE,{"derivedFrom":sQuery(id+"F12.wireOp",EDGE,"E17.2.19.0")}),1.0]])]});
            var Q21;
            Q21=makeQuery(id+"F12.imprint","IMPRINT",FACE,{"disambiguationData":[TD([[makeQuery(id+"F12.imprint","IMPRINT",EDGE,{"derivedFrom":sQuery(id+"F12.wireOp",EDGE,"E17.2.18.0")}),1.0]])]});
            var Q22;
            Q22=makeQuery(id+"F12.imprint","IMPRINT",FACE,{"disambiguationData":[TD([[makeQuery(id+"F12.imprint","IMPRINT",EDGE,{"derivedFrom":sQuery(id+"F12.wireOp",EDGE,"E17.2.17.0")}),1.0]])]});
            var Q23;
            Q23=makeQuery(id+"F12.imprint","IMPRINT",FACE,{"disambiguationData":[TD([[makeQuery(id+"F12.imprint","IMPRINT",EDGE,{"derivedFrom":sQuery(id+"F12.wireOp",EDGE,"E13")}),1.0]])]});
            extrude(context, id + "F16", {"entities" : qUnion([Q0, Q1, Q2, Q3, Q4, Q5, Q6, Q7, Q8, Q9, Q10, Q11, Q12, Q13, Q14, Q15, Q16, Q17, Q18, Q19, Q20, Q21, Q22, Q23]), "operationType" : NewBodyOperationType.REMOVE, "oppositeDirection" : true, "depth" : 12.7 * mm});
        }
        {
            var Q0;
            {var subQ0=sQuery(id+"F12.wireOp",EDGE,"E22.6.30.0");Q0=makeQuery(id+"F12.imprint","IMPRINT",FACE,{"disambiguationData":[TD([[makeQuery(id+"F12.imprint","IMPRINT",EDGE,{"derivedFrom":subQ0}),-1.0]])]});}
            var Q1;
            {var subQ0=sQuery(id+"F12.wireOp",EDGE,"E22.6.29.0");Q1=makeQuery(id+"F12.imprint","IMPRINT",FACE,{"disambiguationData":[TD([[makeQuery(id+"F12.imprint","IMPRINT",EDGE,{"derivedFrom":subQ0}),-1.0]])]});}
            var Q2;
            Q2=makeQuery(id+"F12.imprint","IMPRINT",FACE,{"disambiguationData":[TD([[makeQuery(id+"F12.imprint","IMPRINT",EDGE,{"derivedFrom":sQuery(id+"F12.wireOp",EDGE,"E22.1.28.0")}),-1.0]])]});
            var Q3;
            Q3=makeQuery(id+"F12.imprint","IMPRINT",FACE,{"disambiguationData":[TD([[makeQuery(id+"F12.imprint","IMPRINT",EDGE,{"derivedFrom":sQuery(id+"F12.wireOp",EDGE,"E22.1.27.0")}),-1.0]])]});
            var Q4;
            Q4=makeQuery(id+"F12.imprint","IMPRINT",FACE,{"disambiguationData":[TD([[makeQuery(id+"F12.imprint","IMPRINT",EDGE,{"derivedFrom":sQuery(id+"F12.wireOp",EDGE,"E22.1.26.0")}),-1.0]])]});
            var Q5;
            Q5=makeQuery(id+"F12.imprint","IMPRINT",FACE,{"disambiguationData":[TD([[makeQuery(id+"F12.imprint","IMPRINT",EDGE,{"derivedFrom":sQuery(id+"F12.wireOp",EDGE,"E22.1.25.0")}),-1.0]])]});
            var Q6;
            Q6=makeQuery(id+"F12.imprint","IMPRINT",FACE,{"disambiguationData":[TD([[makeQuery(id+"F12.imprint","IMPRINT",EDGE,{"derivedFrom":sQuery(id+"F12.wireOp",EDGE,"E22.1.23.0")}),-1.0]])]});
            var Q7;
            Q7=makeQuery(id+"F12.imprint","IMPRINT",FACE,{"disambiguationData":[TD([[makeQuery(id+"F12.imprint","IMPRINT",EDGE,{"derivedFrom":sQuery(id+"F12.wireOp",EDGE,"E22.1.24.0")}),-1.0]])]});
            var Q8;
            Q8=makeQuery(id+"F12.imprint","IMPRINT",FACE,{"disambiguationData":[TD([[makeQuery(id+"F12.imprint","IMPRINT",EDGE,{"derivedFrom":sQuery(id+"F12.wireOp",EDGE,"E22.1.22.0")}),-1.0]])]});
            var Q9;
            Q9=makeQuery(id+"F12.imprint","IMPRINT",FACE,{"disambiguationData":[TD([[makeQuery(id+"F12.imprint","IMPRINT",EDGE,{"derivedFrom":sQuery(id+"F12.wireOp",EDGE,"E22.1.21.0")}),-1.0]])]});
            var Q10;
            Q10=makeQuery(id+"F12.imprint","IMPRINT",FACE,{"disambiguationData":[TD([[makeQuery(id+"F12.imprint","IMPRINT",EDGE,{"derivedFrom":sQuery(id+"F12.wireOp",EDGE,"E22.1.20.0")}),-1.0]])]});
            var Q11;
            {var subQ0=sQuery(id+"F12.wireOp",EDGE,"E22.6.19.0");var subQ1=sQuery(id+"F12.wireOp",EDGE,"E22.1.19.0");var subQ2=makeQuery(id+"F12.imprint","INTERSECT",VERTEX,{"derivedFrom":[subQ1,subQ0]});Q11=makeQuery(id+"F12.imprint","IMPRINT",FACE,{"disambiguationData":[TD([[makeQuery(id+"F12.imprint","IMPRINT",EDGE,{"disambiguationData":[TD([[subQ2,-1.0]])],"derivedFrom":subQ1}),-1.0]])]});}
            var Q12;
            {var subQ0=sQuery(id+"F12.wireOp",EDGE,"E22.6.18.0");var subQ1=sQuery(id+"F12.wireOp",EDGE,"E22.1.18.0");var subQ2=makeQuery(id+"F12.imprint","INTERSECT",VERTEX,{"derivedFrom":[subQ1,subQ0]});Q12=makeQuery(id+"F12.imprint","IMPRINT",FACE,{"disambiguationData":[TD([[makeQuery(id+"F12.imprint","IMPRINT",EDGE,{"disambiguationData":[TD([[subQ2,-1.0]])],"derivedFrom":subQ1}),-1.0]])]});}
            var Q13;
            {var subQ0=sQuery(id+"F12.wireOp",EDGE,"E22.6.14.0");Q13=makeQuery(id+"F12.imprint","IMPRINT",FACE,{"disambiguationData":[TD([[makeQuery(id+"F12.imprint","IMPRINT",EDGE,{"derivedFrom":subQ0}),-1.0]])]});}
            var Q14;
            Q14=makeQuery(id+"F12.imprint","IMPRINT",FACE,{"disambiguationData":[TD([[makeQuery(id+"F12.imprint","IMPRINT",EDGE,{"derivedFrom":sQuery(id+"F12.wireOp",EDGE,"E22.1.12.0")}),-1.0]])]});
            var Q15;
            Q15=makeQuery(id+"F12.imprint","IMPRINT",FACE,{"disambiguationData":[TD([[makeQuery(id+"F12.imprint","IMPRINT",EDGE,{"derivedFrom":sQuery(id+"F12.wireOp",EDGE,"E22.1.11.0")}),-1.0]])]});
            var Q16;
            Q16=makeQuery(id+"F12.imprint","IMPRINT",FACE,{"disambiguationData":[TD([[makeQuery(id+"F12.imprint","IMPRINT",EDGE,{"derivedFrom":sQuery(id+"F12.wireOp",EDGE,"E22.1.10.0")}),-1.0]])]});
            var Q17;
            Q17=makeQuery(id+"F12.imprint","IMPRINT",FACE,{"disambiguationData":[TD([[makeQuery(id+"F12.imprint","IMPRINT",EDGE,{"derivedFrom":sQuery(id+"F12.wireOp",EDGE,"E22.1.9.0")}),-1.0]])]});
            var Q18;
            Q18=makeQuery(id+"F12.imprint","IMPRINT",FACE,{"disambiguationData":[TD([[makeQuery(id+"F12.imprint","IMPRINT",EDGE,{"derivedFrom":sQuery(id+"F12.wireOp",EDGE,"E22.1.8.0")}),-1.0]])]});
            var Q19;
            Q19=makeQuery(id+"F12.imprint","IMPRINT",FACE,{"disambiguationData":[TD([[makeQuery(id+"F12.imprint","IMPRINT",EDGE,{"derivedFrom":sQuery(id+"F12.wireOp",EDGE,"E22.1.7.0")}),-1.0]])]});
            var Q20;
            Q20=makeQuery(id+"F12.imprint","IMPRINT",FACE,{"disambiguationData":[TD([[makeQuery(id+"F12.imprint","IMPRINT",EDGE,{"derivedFrom":sQuery(id+"F12.wireOp",EDGE,"E22.1.6.0")}),-1.0]])]});
            var Q21;
            Q21=makeQuery(id+"F12.imprint","IMPRINT",FACE,{"disambiguationData":[TD([[makeQuery(id+"F12.imprint","IMPRINT",EDGE,{"derivedFrom":sQuery(id+"F12.wireOp",EDGE,"E22.1.5.0")}),-1.0]])]});
            var Q22;
            Q22=makeQuery(id+"F12.imprint","IMPRINT",FACE,{"disambiguationData":[TD([[makeQuery(id+"F12.imprint","IMPRINT",EDGE,{"derivedFrom":sQuery(id+"F12.wireOp",EDGE,"E22.1.4.0")}),-1.0]])]});
            var Q23;
            {var subQ0=sQuery(id+"F12.wireOp",EDGE,"E22.6.12.0");Q23=makeQuery(id+"F12.imprint","IMPRINT",FACE,{"disambiguationData":[TD([[makeQuery(id+"F12.imprint","IMPRINT",EDGE,{"derivedFrom":subQ0}),-1.0]])]});}
            var Q24;
            {var subQ0=sQuery(id+"F12.wireOp",EDGE,"E22.6.27.0");Q24=makeQuery(id+"F12.imprint","IMPRINT",FACE,{"disambiguationData":[TD([[makeQuery(id+"F12.imprint","IMPRINT",EDGE,{"derivedFrom":subQ0}),-1.0]])]});}
            var Q25;
            {var subQ0=sQuery(id+"F12.wireOp",EDGE,"E22.6.3.0");var subQ1=sQuery(id+"F12.wireOp",EDGE,"E22.1.3.0");var subQ2=makeQuery(id+"F12.imprint","INTERSECT",VERTEX,{"derivedFrom":[subQ1,subQ0]});Q25=makeQuery(id+"F12.imprint","IMPRINT",FACE,{"disambiguationData":[TD([[makeQuery(id+"F12.imprint","IMPRINT",EDGE,{"disambiguationData":[TD([[subQ2,-1.0]])],"derivedFrom":subQ1}),-1.0]])]});}
            extrude(context, id + "F17", {"entities" : qUnion([Q0, Q1, Q2, Q3, Q4, Q5, Q6, Q7, Q8, Q9, Q10, Q11, Q12, Q13, Q14, Q15, Q16, Q17, Q18, Q19, Q20, Q21, Q22, Q23, Q24, Q25]), "operationType" : NewBodyOperationType.REMOVE, "oppositeDirection" : true, "depth" : 19.05 * mm});
        }
        {
            var Q0;
            {var subQ0=sQuery(id+"F12.wireOp",EDGE,"E27.6.8.0");Q0=makeQuery(id+"F12.imprint","IMPRINT",FACE,{"disambiguationData":[TD([[makeQuery(id+"F12.imprint","IMPRINT",EDGE,{"derivedFrom":subQ0}),1.0]])]});}
            var Q1;
            {var subQ0=sQuery(id+"F12.wireOp",EDGE,"E27.6.9.0");Q1=makeQuery(id+"F12.imprint","IMPRINT",FACE,{"disambiguationData":[TD([[makeQuery(id+"F12.imprint","IMPRINT",EDGE,{"derivedFrom":subQ0}),1.0]])]});}
            var Q2;
            {var subQ0=sQuery(id+"F12.wireOp",EDGE,"E27.6.10.0");Q2=makeQuery(id+"F12.imprint","IMPRINT",FACE,{"disambiguationData":[TD([[makeQuery(id+"F12.imprint","IMPRINT",EDGE,{"derivedFrom":subQ0}),1.0]])]});}
            var Q3;
            Q3=makeQuery(id+"F12.imprint","IMPRINT",FACE,{"disambiguationData":[TD([[makeQuery(id+"F12.imprint","IMPRINT",EDGE,{"derivedFrom":sQuery(id+"F12.wireOp",EDGE,"E27.1.11.0")}),1.0]])]});
            var Q4;
            Q4=makeQuery(id+"F12.imprint","IMPRINT",FACE,{"disambiguationData":[TD([[makeQuery(id+"F12.imprint","IMPRINT",EDGE,{"derivedFrom":sQuery(id+"F12.wireOp",EDGE,"E27.1.12.0")}),1.0]])]});
            var Q5;
            {var subQ0=sQuery(id+"F12.wireOp",EDGE,"E27.6.22.0");var subQ1=sQuery(id+"F12.wireOp",EDGE,"E27.3.22.0");var subQ2=makeQuery(id+"F12.imprint","INTERSECT",VERTEX,{"derivedFrom":[subQ1,subQ0]});Q5=makeQuery(id+"F12.imprint","IMPRINT",FACE,{"disambiguationData":[TD([[makeQuery(id+"F12.imprint","IMPRINT",EDGE,{"disambiguationData":[TD([[subQ2,1.0]])],"derivedFrom":subQ1}),1.0]])]});}
            var Q6;
            Q6=makeQuery(id+"F12.imprint","IMPRINT",FACE,{"disambiguationData":[TD([[makeQuery(id+"F12.imprint","IMPRINT",EDGE,{"derivedFrom":sQuery(id+"F12.wireOp",EDGE,"E27.1.23.0")}),1.0]])]});
            var Q7;
            Q7=makeQuery(id+"F12.imprint","IMPRINT",FACE,{"disambiguationData":[TD([[makeQuery(id+"F12.imprint","IMPRINT",EDGE,{"derivedFrom":sQuery(id+"F12.wireOp",EDGE,"E27.1.24.0")}),1.0]])]});
            var Q8;
            Q8=makeQuery(id+"F12.imprint","IMPRINT",FACE,{"disambiguationData":[TD([[makeQuery(id+"F12.imprint","IMPRINT",EDGE,{"derivedFrom":sQuery(id+"F12.wireOp",EDGE,"E27.1.25.0")}),1.0]])]});
            var Q9;
            {var subQ0=sQuery(id+"F12.wireOp",EDGE,"E27.6.26.0");Q9=makeQuery(id+"F12.imprint","IMPRINT",FACE,{"disambiguationData":[TD([[makeQuery(id+"F12.imprint","IMPRINT",EDGE,{"derivedFrom":subQ0}),1.0]])]});}
            var Q10;
            {var subQ0=sQuery(id+"F12.wireOp",EDGE,"E27.6.27.0");Q10=makeQuery(id+"F12.imprint","IMPRINT",FACE,{"disambiguationData":[TD([[makeQuery(id+"F12.imprint","IMPRINT",EDGE,{"derivedFrom":subQ0}),1.0]])]});}
            var Q11;
            {var subQ0=sQuery(id+"F12.wireOp",EDGE,"E27.6.28.0");Q11=makeQuery(id+"F12.imprint","IMPRINT",FACE,{"disambiguationData":[TD([[makeQuery(id+"F12.imprint","IMPRINT",EDGE,{"derivedFrom":subQ0}),1.0]])]});}
            var Q12;
            Q12=makeQuery(id+"F12.imprint","IMPRINT",FACE,{"disambiguationData":[TD([[makeQuery(id+"F12.imprint","IMPRINT",EDGE,{"derivedFrom":sQuery(id+"F12.wireOp",EDGE,"E27.1.29.0")}),1.0]])]});
            var Q13;
            Q13=makeQuery(id+"F12.imprint","IMPRINT",FACE,{"disambiguationData":[TD([[makeQuery(id+"F12.imprint","IMPRINT",EDGE,{"derivedFrom":sQuery(id+"F12.wireOp",EDGE,"E27.1.5.0")}),1.0]])]});
            var Q14;
            Q14=makeQuery(id+"F12.imprint","IMPRINT",FACE,{"disambiguationData":[TD([[makeQuery(id+"F12.imprint","IMPRINT",EDGE,{"derivedFrom":sQuery(id+"F12.wireOp",EDGE,"E27.1.6.0")}),1.0]])]});
            var Q15;
            Q15=makeQuery(id+"F12.imprint","IMPRINT",FACE,{"disambiguationData":[TD([[makeQuery(id+"F12.imprint","IMPRINT",EDGE,{"derivedFrom":sQuery(id+"F12.wireOp",EDGE,"E27.1.7.0")}),1.0]])]});
            var Q16;
            {var subQ0=sQuery(id+"F12.wireOp",EDGE,"E27.6.25.0");Q16=makeQuery(id+"F12.imprint","IMPRINT",FACE,{"disambiguationData":[TD([[makeQuery(id+"F12.imprint","IMPRINT",EDGE,{"derivedFrom":subQ0}),1.0]])]});}
            extrude(context, id + "F18", {"entities" : qUnion([Q0, Q1, Q2, Q3, Q4, Q5, Q6, Q7, Q8, Q9, Q10, Q11, Q12, Q13, Q14, Q15, Q16]), "operationType" : NewBodyOperationType.REMOVE, "oppositeDirection" : true, "depth" : 25.4 * mm});
        }
        {
            var Q0;
            {var subQ60=sQuery(id+"F12.wireOp",EDGE,"E4");Q0=makeQuery(id+"F12.imprint","IMPRINT",FACE,{"disambiguationData":[TD([[makeQuery(id+"F12.imprint","IMPRINT",EDGE,{"derivedFrom":subQ60}),1.0]])]});}
            var sketch = newSketch(context, id + "F19", { "sketchPlane" : qUnion([Q0])});
            skArc(sketch, "E33", {"start": v(-38.1, 19.05) * mm, "mid": v(-33.6, 20.9) * mm, "end": v(-31.75, 25.4) * mm});
            skCircle(sketch, "E34", {"center": v(-35.85, 23.15) * mm, "radius": 1.9 * mm});
            skLineSegment(sketch, "E35", {"start": v(-38.1, 25.4) * mm, "end": v(-33.6, 20.9) * mm});
            skSolve(sketch);
        }
        {
            var Q0;
            {var subQ0=sQuery(id+"F19.wireOp",EDGE,"E35");var subQ3=sQuery(id+"F19.wireOp",EDGE,"E34");var subQ10=makeQuery(id+"F19.imprint","INTERSECT",VERTEX,{"disambiguationData":[OD(0.0)],"derivedFrom":[subQ3,subQ0]});Q0=makeQuery(id+"F19.imprint","IMPRINT",FACE,{"disambiguationData":[TD([[makeQuery(id+"F19.imprint","IMPRINT",EDGE,{"disambiguationData":[TD([[subQ10,-1.0]])],"derivedFrom":subQ3}),-1.0]])]});}
            var Q1;
            {var subQ0=sQuery(id+"F19.wireOp",EDGE,"E35");var subQ6=sQuery(id+"F19.wireOp",EDGE,"E34");var subQ7=makeQuery(id+"F19.imprint","INTERSECT",VERTEX,{"disambiguationData":[OD(0.0)],"derivedFrom":[subQ6,subQ0]});Q1=makeQuery(id+"F19.imprint","IMPRINT",FACE,{"disambiguationData":[TD([[makeQuery(id+"F19.imprint","IMPRINT",EDGE,{"disambiguationData":[TD([[subQ7,1.0]])],"derivedFrom":subQ6}),-1.0]])]});}
            extrude(context, id + "F20", {"entities" : qUnion([Q0, Q1]), "operationType" : NewBodyOperationType.REMOVE, "oppositeDirection" : true, "depth" : 15.88 * mm});
        }
        {
            var Q0;
            {var subQ0=sQuery(id+"F19.wireOp",EDGE,"E35");var subQ1=sQuery(id+"F19.wireOp",EDGE,"E34");var subQ2=makeQuery(id+"F19.imprint","INTERSECT",VERTEX,{"disambiguationData":[OD(0.0)],"derivedFrom":[subQ1,subQ0]});Q0=makeQuery(id+"F19.imprint","IMPRINT",FACE,{"disambiguationData":[TD([[makeQuery(id+"F19.imprint","IMPRINT",EDGE,{"disambiguationData":[TD([[subQ2,-1.0]])],"derivedFrom":subQ1}),1.0]])]});}
            var Q1;
            {var subQ0=sQuery(id+"F19.wireOp",EDGE,"E35");var subQ1=sQuery(id+"F19.wireOp",EDGE,"E34");var subQ2=makeQuery(id+"F19.imprint","INTERSECT",VERTEX,{"disambiguationData":[OD(0.0)],"derivedFrom":[subQ1,subQ0]});Q1=makeQuery(id+"F19.imprint","IMPRINT",FACE,{"disambiguationData":[TD([[makeQuery(id+"F19.imprint","IMPRINT",EDGE,{"disambiguationData":[TD([[subQ2,1.0]])],"derivedFrom":subQ1}),1.0]])]});}
            extrude(context, id + "F21", {"entities" : qUnion([Q0, Q1]), "operationType" : NewBodyOperationType.REMOVE, "oppositeDirection" : true, "depth" : 25.9 * mm});
        }
        {
            var Q0;
            Q0=makeQuery(id+"F1.opExtrude","CAP_FACE",FACE,{"disambiguationData":[OSD([sQuery(id+"F0.wireOp",EDGE,"E0.bottom"),sQuery(id+"F0.wireOp",EDGE,"E0.top"),sQuery(id+"F0.wireOp",EDGE,"E0.left"),sQuery(id+"F0.wireOp",EDGE,"E0.right")])],"isStart":false});
            var sketch = newSketch(context, id + "F22", { "sketchPlane" : qUnion([Q0])});
            skArc(sketch, "E36", {"start": v(-31.75, -25.4) * mm, "mid": v(-33.6, -20.9) * mm, "end": v(-38.1, -19.05) * mm});
            skLineSegment(sketch, "E37", {"start": v(-38.1, -25.4) * mm, "end": v(-33.6, -20.9) * mm});
            skCircle(sketch, "E38", {"center": v(-35.85, -23.15) * mm, "radius": 1.65 * mm});
            skSolve(sketch);
        }
        {
            var Q0;
            {var subQ0=sQuery(id+"F22.wireOp",EDGE,"E38");var subQ1=sQuery(id+"F22.wireOp",EDGE,"E37");var subQ2=makeQuery(id+"F22.imprint","INTERSECT",VERTEX,{"disambiguationData":[OD(0.0)],"derivedFrom":[subQ1,subQ0]});Q0=makeQuery(id+"F22.imprint","IMPRINT",FACE,{"disambiguationData":[TD([[makeQuery(id+"F22.imprint","IMPRINT",EDGE,{"disambiguationData":[TD([[subQ2,-1.0]])],"derivedFrom":subQ1}),1.0]])]});}
            var Q1;
            {var subQ0=sQuery(id+"F22.wireOp",EDGE,"E38");var subQ1=sQuery(id+"F22.wireOp",EDGE,"E37");var subQ2=makeQuery(id+"F22.imprint","INTERSECT",VERTEX,{"disambiguationData":[OD(0.0)],"derivedFrom":[subQ1,subQ0]});Q1=makeQuery(id+"F22.imprint","IMPRINT",FACE,{"disambiguationData":[TD([[makeQuery(id+"F22.imprint","IMPRINT",EDGE,{"disambiguationData":[TD([[subQ2,-1.0]])],"derivedFrom":subQ1}),-1.0]])]});}
            extrude(context, id + "F23", {"entities" : qUnion([Q0, Q1]), "operationType" : NewBodyOperationType.ADD, "depth" : 25.4 * mm});
        }
        {
            var Q0;
            {var subQ4=sQuery(id+"F22.wireOp",EDGE,"E36");var subQ6=makeQuery(id+"F1.opExtrude","CAP_EDGE",EDGE,{"disambiguationData":[OSD([sQuery(id+"F0.wireOp",EDGE,"E0.left")])],"isStart":false});var subQ8=makeQuery(id+"F22.imprint","INTERSECT",VERTEX,{"derivedFrom":[subQ6,subQ4]});Q0=makeQuery(id+"F22.imprint","IMPRINT",FACE,{"disambiguationData":[TD([[makeQuery(id+"F22.imprint","IMPRINT",EDGE,{"disambiguationData":[TD([[subQ8,1.0]])],"derivedFrom":subQ4}),1.0]])]});}
            var Q1;
            {var subQ4=sQuery(id+"F22.wireOp",EDGE,"E36");var subQ6=makeQuery(id+"F1.opExtrude","CAP_EDGE",EDGE,{"disambiguationData":[OSD([sQuery(id+"F0.wireOp",EDGE,"E0.top")])],"isStart":false});var subQ8=makeQuery(id+"F22.imprint","INTERSECT",VERTEX,{"derivedFrom":[subQ6,subQ4]});Q1=makeQuery(id+"F22.imprint","IMPRINT",FACE,{"disambiguationData":[TD([[makeQuery(id+"F22.imprint","IMPRINT",EDGE,{"disambiguationData":[TD([[subQ8,-1.0]])],"derivedFrom":subQ4}),1.0]])]});}
            extrude(context, id + "F24", {"entities" : qUnion([Q0, Q1]), "operationType" : NewBodyOperationType.ADD, "depth" : 15.82 * mm});
        }
        {
            var Q0;
            {var subQ80=sQuery(id+"F12.wireOp",EDGE,"E4");Q0=makeQuery(id+"F19.imprint","IMPRINT",FACE,{"disambiguationData":[TD([[makeQuery(id+"F19.imprint","IMPRINT",EDGE,{"derivedFrom":makeQuery(id+"F12.imprint","IMPRINT",EDGE,{"derivedFrom":subQ80})}),1.0]])]});}
            var sketch = newSketch(context, id + "F25", { "sketchPlane" : qUnion([Q0])});
            skLineSegment(sketch, "E39", {"start": v(38.1, -18.8) * mm, "end": v(28.28, -25.4) * mm});
            skPoint(sketch, "E40.left.end.orphan", {"position": v(38.1, -19.46) * mm});
            skPoint(sketch, "E40.left.start.orphan", {"position": v(38.1, -22) * mm});
            skSolve(sketch);
        }
        {
            var Q0;
            {var subQ1=sQuery(id+"F25.wireOp",EDGE,"E39");Q0=makeQuery(id+"F25.imprint","IMPRINT",FACE,{"disambiguationData":[TD([[makeQuery(id+"F25.imprint","IMPRINT",EDGE,{"derivedFrom":subQ1}),1.0]])]});}
            extrude(context, id + "F26", {"entities" : qUnion([Q0]), "operationType" : NewBodyOperationType.REMOVE, "oppositeDirection" : true, "depth" : 12.7 * mm});
        }
        {
            var Q0;
            {var subQ1=makeQuery(id+"F1.opExtrude","CAP_EDGE",EDGE,{"disambiguationData":[OSD([sQuery(id+"F0.wireOp",EDGE,"E0.bottom")])],"isStart":false});Q0=makeQuery(id+"F22.imprint","IMPRINT",FACE,{"disambiguationData":[TD([[makeQuery(id+"F22.imprint","IMPRINT",EDGE,{"derivedFrom":subQ1}),-1.0]])]});}
            var sketch = newSketch(context, id + "F27", { "sketchPlane" : qUnion([Q0])});
            skLineSegment(sketch, "E41", {"start": v(28.28, 25.4) * mm, "end": v(38.1, 18.8) * mm});
            skSolve(sketch);
        }
        {
            var Q0;
            Q0=makeQuery(id+"F1.opExtrude","CAP_FACE",FACE,{"disambiguationData":[OSD([sQuery(id+"F0.wireOp",EDGE,"E0.bottom"),sQuery(id+"F0.wireOp",EDGE,"E0.top"),sQuery(id+"F0.wireOp",EDGE,"E0.left"),sQuery(id+"F0.wireOp",EDGE,"E0.right")])],"isStart":false});
            var sketch = newSketch(context, id + "F28", { "sketchPlane" : qUnion([Q0])});
            skLineSegment(sketch, "E42", {"start": v(0, 0) * mm, "end": v(0, 13.08) * mm});
            skLineSegment(sketch, "E43", {"start": v(0, 13.08) * mm, "end": v(0, 17.4) * mm});
            skLineSegment(sketch, "E44", {"start": v(0, 17.4) * mm, "end": v(-3.74, 15.24) * mm});
            skLineSegment(sketch, "E45", {"start": v(-3.74, 15.24) * mm, "end": v(0, 13.08) * mm});
            skLineSegment(sketch, "E46", {"start": v(0, 20.07) * mm, "end": v(0, 24.38) * mm});
            skLineSegment(sketch, "E47", {"start": v(0, 24.38) * mm, "end": v(3.74, 22.23) * mm});
            skLineSegment(sketch, "E48", {"start": v(3.74, 22.23) * mm, "end": v(0, 20.07) * mm});
            skLineSegment(sketch, "E49", {"start": v(0, 27.05) * mm, "end": v(0, 31.37) * mm});
            skLineSegment(sketch, "E50", {"start": v(0, 31.37) * mm, "end": v(-3.74, 29.21) * mm});
            skLineSegment(sketch, "E51", {"start": v(-3.74, 29.21) * mm, "end": v(0, 27.05) * mm});
            skLineSegment(sketch, "E52", {"start": v(0, 34.04) * mm, "end": v(0, 38.35) * mm});
            skLineSegment(sketch, "E53", {"start": v(0, 38.35) * mm, "end": v(3.74, 36.2) * mm});
            skLineSegment(sketch, "E54", {"start": v(3.74, 36.2) * mm, "end": v(0, 34.04) * mm});
            skLineSegment(sketch, "E55.1.0", {"start": v(-6.66, 16.07) * mm, "end": v(-9.29, 12.65) * mm});
            skLineSegment(sketch, "E55.1.1", {"start": v(-5, 12.09) * mm, "end": v(-6.66, 16.07) * mm});
            skLineSegment(sketch, "E55.1.2", {"start": v(-9.29, 12.65) * mm, "end": v(-5, 12.09) * mm});
            skLineSegment(sketch, "E55.2.0", {"start": v(-12.3, 12.3) * mm, "end": v(-13.42, 8.13) * mm});
            skLineSegment(sketch, "E55.2.1", {"start": v(-9.25, 9.25) * mm, "end": v(-12.3, 12.3) * mm});
            skLineSegment(sketch, "E55.2.2", {"start": v(-13.42, 8.13) * mm, "end": v(-9.25, 9.25) * mm});
            skPoint(sketch, "E55.center", {"position": v(0, 0) * mm});
            skLineSegment(sketch, "E56.2.3.0", {"start": v(-16.07, 6.66) * mm, "end": v(-15.51, 2.38) * mm});
            skLineSegment(sketch, "E56.3.3.0", {"start": v(-12.09, 5) * mm, "end": v(-16.07, 6.66) * mm});
            skLineSegment(sketch, "E56.6.3.0", {"start": v(-15.51, 2.38) * mm, "end": v(-12.09, 5) * mm});
            skLineSegment(sketch, "E56.2.4.0", {"start": v(-17.4, 0) * mm, "end": v(-15.24, -3.74) * mm});
            skLineSegment(sketch, "E56.3.4.0", {"start": v(-13.08, 0) * mm, "end": v(-17.4, 0) * mm});
            skLineSegment(sketch, "E56.6.4.0", {"start": v(-15.24, -3.74) * mm, "end": v(-13.08, 0) * mm});
            skLineSegment(sketch, "E56.2.5.0", {"start": v(-16.07, -6.66) * mm, "end": v(-12.65, -9.29) * mm});
            skLineSegment(sketch, "E56.3.5.0", {"start": v(-12.09, -5) * mm, "end": v(-16.07, -6.66) * mm});
            skLineSegment(sketch, "E56.6.5.0", {"start": v(-12.65, -9.29) * mm, "end": v(-12.09, -5) * mm});
            skLineSegment(sketch, "E56.2.6.0", {"start": v(-12.3, -12.3) * mm, "end": v(-8.13, -13.42) * mm});
            skLineSegment(sketch, "E56.3.6.0", {"start": v(-9.25, -9.25) * mm, "end": v(-12.3, -12.3) * mm});
            skLineSegment(sketch, "E56.6.6.0", {"start": v(-8.13, -13.42) * mm, "end": v(-9.25, -9.25) * mm});
            skLineSegment(sketch, "E56.2.7.0", {"start": v(-6.66, -16.07) * mm, "end": v(-2.38, -15.51) * mm});
            skLineSegment(sketch, "E56.3.7.0", {"start": v(-5, -12.09) * mm, "end": v(-6.66, -16.07) * mm});
            skLineSegment(sketch, "E56.6.7.0", {"start": v(-2.38, -15.51) * mm, "end": v(-5, -12.09) * mm});
            skLineSegment(sketch, "E56.2.8.0", {"start": v(0, -17.4) * mm, "end": v(3.74, -15.24) * mm});
            skLineSegment(sketch, "E56.3.8.0", {"start": v(0, -13.08) * mm, "end": v(0, -17.4) * mm});
            skLineSegment(sketch, "E56.6.8.0", {"start": v(3.74, -15.24) * mm, "end": v(0, -13.08) * mm});
            skLineSegment(sketch, "E56.2.9.0", {"start": v(6.66, -16.07) * mm, "end": v(9.29, -12.65) * mm});
            skLineSegment(sketch, "E56.3.9.0", {"start": v(5, -12.09) * mm, "end": v(6.66, -16.07) * mm});
            skLineSegment(sketch, "E56.6.9.0", {"start": v(9.29, -12.65) * mm, "end": v(5, -12.09) * mm});
            skLineSegment(sketch, "E56.2.10.0", {"start": v(12.3, -12.3) * mm, "end": v(13.42, -8.13) * mm});
            skLineSegment(sketch, "E56.3.10.0", {"start": v(9.25, -9.25) * mm, "end": v(12.3, -12.3) * mm});
            skLineSegment(sketch, "E56.6.10.0", {"start": v(13.42, -8.13) * mm, "end": v(9.25, -9.25) * mm});
            skLineSegment(sketch, "E56.2.11.0", {"start": v(16.07, -6.66) * mm, "end": v(15.51, -2.38) * mm});
            skLineSegment(sketch, "E56.3.11.0", {"start": v(12.09, -5) * mm, "end": v(16.07, -6.66) * mm});
            skLineSegment(sketch, "E56.6.11.0", {"start": v(15.51, -2.38) * mm, "end": v(12.09, -5) * mm});
            skLineSegment(sketch, "E57.1.0", {"start": v(-2.14, 22.44) * mm, "end": v(-5.2, 19.38) * mm});
            skLineSegment(sketch, "E57.1.1", {"start": v(-5.2, 19.38) * mm, "end": v(-6.31, 23.55) * mm});
            skLineSegment(sketch, "E57.1.2", {"start": v(-6.31, 23.55) * mm, "end": v(-2.14, 22.44) * mm});
            skLineSegment(sketch, "E57.2.0", {"start": v(-7.87, 21.12) * mm, "end": v(-10.03, 17.38) * mm});
            skLineSegment(sketch, "E57.2.1", {"start": v(-10.03, 17.38) * mm, "end": v(-12.2, 21.12) * mm});
            skLineSegment(sketch, "E57.2.2", {"start": v(-12.2, 21.12) * mm, "end": v(-7.87, 21.12) * mm});
            skLineSegment(sketch, "E58.2.3.0", {"start": v(-13.07, 18.36) * mm, "end": v(-14.19, 14.19) * mm});
            skLineSegment(sketch, "E58.3.3.0", {"start": v(-14.19, 14.19) * mm, "end": v(-17.24, 17.24) * mm});
            skLineSegment(sketch, "E58.6.3.0", {"start": v(-17.24, 17.24) * mm, "end": v(-13.07, 18.36) * mm});
            skLineSegment(sketch, "E58.2.4.0", {"start": v(-17.38, 14.35) * mm, "end": v(-17.38, 10.03) * mm});
            skLineSegment(sketch, "E58.3.4.0", {"start": v(-17.38, 10.03) * mm, "end": v(-21.12, 12.2) * mm});
            skLineSegment(sketch, "E58.6.4.0", {"start": v(-21.12, 12.2) * mm, "end": v(-17.38, 14.35) * mm});
            skLineSegment(sketch, "E58.2.5.0", {"start": v(-20.5, 9.36) * mm, "end": v(-19.38, 5.2) * mm});
            skLineSegment(sketch, "E58.3.5.0", {"start": v(-19.38, 5.2) * mm, "end": v(-23.55, 6.31) * mm});
            skLineSegment(sketch, "E58.6.5.0", {"start": v(-23.55, 6.31) * mm, "end": v(-20.5, 9.36) * mm});
            skLineSegment(sketch, "E58.2.6.0", {"start": v(-22.23, 3.74) * mm, "end": v(-20.07, 0) * mm});
            skLineSegment(sketch, "E58.3.6.0", {"start": v(-20.07, 0) * mm, "end": v(-24.38, 0) * mm});
            skLineSegment(sketch, "E58.6.6.0", {"start": v(-24.38, 0) * mm, "end": v(-22.23, 3.74) * mm});
            skLineSegment(sketch, "E58.2.7.0", {"start": v(-22.44, -2.14) * mm, "end": v(-19.38, -5.2) * mm});
            skLineSegment(sketch, "E58.3.7.0", {"start": v(-19.38, -5.2) * mm, "end": v(-23.55, -6.31) * mm});
            skLineSegment(sketch, "E58.6.7.0", {"start": v(-23.55, -6.31) * mm, "end": v(-22.44, -2.14) * mm});
            skLineSegment(sketch, "E58.2.8.0", {"start": v(-21.12, -7.87) * mm, "end": v(-17.38, -10.03) * mm});
            skLineSegment(sketch, "E58.3.8.0", {"start": v(-17.38, -10.03) * mm, "end": v(-21.12, -12.2) * mm});
            skLineSegment(sketch, "E58.6.8.0", {"start": v(-21.12, -12.2) * mm, "end": v(-21.12, -7.87) * mm});
            skLineSegment(sketch, "E58.2.9.0", {"start": v(-18.36, -13.07) * mm, "end": v(-14.19, -14.19) * mm});
            skLineSegment(sketch, "E58.3.9.0", {"start": v(-14.19, -14.19) * mm, "end": v(-17.24, -17.24) * mm});
            skLineSegment(sketch, "E58.6.9.0", {"start": v(-17.24, -17.24) * mm, "end": v(-18.36, -13.07) * mm});
            skLineSegment(sketch, "E58.2.10.0", {"start": v(-14.35, -17.38) * mm, "end": v(-10.03, -17.38) * mm});
            skLineSegment(sketch, "E58.3.10.0", {"start": v(-10.03, -17.38) * mm, "end": v(-12.2, -21.12) * mm});
            skLineSegment(sketch, "E58.6.10.0", {"start": v(-12.2, -21.12) * mm, "end": v(-14.35, -17.38) * mm});
            skLineSegment(sketch, "E58.2.11.0", {"start": v(-9.36, -20.5) * mm, "end": v(-5.2, -19.38) * mm});
            skLineSegment(sketch, "E58.3.11.0", {"start": v(-5.2, -19.38) * mm, "end": v(-6.31, -23.55) * mm});
            skLineSegment(sketch, "E58.6.11.0", {"start": v(-6.31, -23.55) * mm, "end": v(-9.36, -20.5) * mm});
            skLineSegment(sketch, "E58.2.12.0", {"start": v(-3.74, -22.23) * mm, "end": v(0, -20.07) * mm});
            skLineSegment(sketch, "E58.3.12.0", {"start": v(0, -20.07) * mm, "end": v(0, -24.38) * mm});
            skLineSegment(sketch, "E58.6.12.0", {"start": v(0, -24.38) * mm, "end": v(-3.74, -22.23) * mm});
            skLineSegment(sketch, "E58.2.13.0", {"start": v(2.14, -22.44) * mm, "end": v(5.2, -19.38) * mm});
            skLineSegment(sketch, "E58.3.13.0", {"start": v(5.2, -19.38) * mm, "end": v(6.31, -23.55) * mm});
            skLineSegment(sketch, "E58.6.13.0", {"start": v(6.31, -23.55) * mm, "end": v(2.14, -22.44) * mm});
            skLineSegment(sketch, "E58.2.14.0", {"start": v(7.87, -21.12) * mm, "end": v(10.03, -17.38) * mm});
            skLineSegment(sketch, "E58.3.14.0", {"start": v(10.03, -17.38) * mm, "end": v(12.2, -21.12) * mm});
            skLineSegment(sketch, "E58.6.14.0", {"start": v(12.2, -21.12) * mm, "end": v(7.87, -21.12) * mm});
            skLineSegment(sketch, "E58.2.15.0", {"start": v(13.07, -18.36) * mm, "end": v(14.19, -14.19) * mm});
            skLineSegment(sketch, "E58.3.15.0", {"start": v(14.19, -14.19) * mm, "end": v(17.24, -17.24) * mm});
            skLineSegment(sketch, "E58.6.15.0", {"start": v(17.24, -17.24) * mm, "end": v(13.07, -18.36) * mm});
            skLineSegment(sketch, "E58.2.16.0", {"start": v(17.38, -14.35) * mm, "end": v(17.38, -10.03) * mm});
            skLineSegment(sketch, "E58.3.16.0", {"start": v(17.38, -10.03) * mm, "end": v(21.12, -12.2) * mm});
            skLineSegment(sketch, "E58.6.16.0", {"start": v(21.12, -12.2) * mm, "end": v(17.38, -14.35) * mm});
            skLineSegment(sketch, "E58.2.17.0", {"start": v(20.5, -9.36) * mm, "end": v(19.38, -5.2) * mm});
            skLineSegment(sketch, "E58.3.17.0", {"start": v(19.38, -5.2) * mm, "end": v(23.55, -6.31) * mm});
            skLineSegment(sketch, "E58.6.17.0", {"start": v(23.55, -6.31) * mm, "end": v(20.5, -9.36) * mm});
            skLineSegment(sketch, "E59.1.0", {"start": v(-5.62, 26.46) * mm, "end": v(-6.52, 30.68) * mm});
            skLineSegment(sketch, "E59.1.1", {"start": v(-6.52, 30.68) * mm, "end": v(-9.73, 27.8) * mm});
            skLineSegment(sketch, "E59.1.2", {"start": v(-9.73, 27.8) * mm, "end": v(-5.62, 26.46) * mm});
            skLineSegment(sketch, "E59.2.0", {"start": v(-11, 24.71) * mm, "end": v(-12.76, 28.66) * mm});
            skLineSegment(sketch, "E59.2.1", {"start": v(-12.76, 28.66) * mm, "end": v(-15.3, 25.16) * mm});
            skLineSegment(sketch, "E59.2.2", {"start": v(-15.3, 25.16) * mm, "end": v(-11, 24.71) * mm});
            skLineSegment(sketch, "E60.1.3.0", {"start": v(-15.9, 21.88) * mm, "end": v(-18.44, 25.38) * mm});
            skLineSegment(sketch, "E60.3.3.0", {"start": v(-18.44, 25.38) * mm, "end": v(-20.2, 21.43) * mm});
            skLineSegment(sketch, "E60.6.3.0", {"start": v(-20.2, 21.43) * mm, "end": v(-15.9, 21.88) * mm});
            skLineSegment(sketch, "E60.1.4.0", {"start": v(-20.1, 18.1) * mm, "end": v(-23.31, 20.99) * mm});
            skLineSegment(sketch, "E60.3.4.0", {"start": v(-23.31, 20.99) * mm, "end": v(-24.2, 16.77) * mm});
            skLineSegment(sketch, "E60.6.4.0", {"start": v(-24.2, 16.77) * mm, "end": v(-20.1, 18.1) * mm});
            skLineSegment(sketch, "E60.1.5.0", {"start": v(-23.43, 13.53) * mm, "end": v(-27.17, 15.68) * mm});
            skLineSegment(sketch, "E60.3.5.0", {"start": v(-27.17, 15.68) * mm, "end": v(-27.17, 11.37) * mm});
            skLineSegment(sketch, "E60.6.5.0", {"start": v(-27.17, 11.37) * mm, "end": v(-23.43, 13.53) * mm});
            skLineSegment(sketch, "E60.1.6.0", {"start": v(-25.73, 8.36) * mm, "end": v(-29.83, 9.7) * mm});
            skLineSegment(sketch, "E60.3.6.0", {"start": v(-29.83, 9.7) * mm, "end": v(-28.94, 5.47) * mm});
            skLineSegment(sketch, "E60.6.6.0", {"start": v(-28.94, 5.47) * mm, "end": v(-25.73, 8.36) * mm});
            skLineSegment(sketch, "E60.1.7.0", {"start": v(-26.9, 2.83) * mm, "end": v(-31.2, 3.28) * mm});
            skLineSegment(sketch, "E60.3.7.0", {"start": v(-31.2, 3.28) * mm, "end": v(-29.44, -0.67) * mm});
            skLineSegment(sketch, "E60.6.7.0", {"start": v(-29.44, -0.67) * mm, "end": v(-26.9, 2.83) * mm});
            skLineSegment(sketch, "E60.1.8.0", {"start": v(-26.9, -2.83) * mm, "end": v(-31.2, -3.28) * mm});
            skLineSegment(sketch, "E60.3.8.0", {"start": v(-31.2, -3.28) * mm, "end": v(-28.66, -6.77) * mm});
            skLineSegment(sketch, "E60.6.8.0", {"start": v(-28.66, -6.77) * mm, "end": v(-26.9, -2.83) * mm});
            skLineSegment(sketch, "E60.1.9.0", {"start": v(-25.73, -8.36) * mm, "end": v(-29.83, -9.7) * mm});
            skLineSegment(sketch, "E60.3.9.0", {"start": v(-29.83, -9.7) * mm, "end": v(-26.62, -12.58) * mm});
            skLineSegment(sketch, "E60.6.9.0", {"start": v(-26.62, -12.58) * mm, "end": v(-25.73, -8.36) * mm});
            skLineSegment(sketch, "E60.1.10.0", {"start": v(-23.43, -13.53) * mm, "end": v(-27.17, -15.68) * mm});
            skLineSegment(sketch, "E60.3.10.0", {"start": v(-27.17, -15.68) * mm, "end": v(-23.43, -17.84) * mm});
            skLineSegment(sketch, "E60.6.10.0", {"start": v(-23.43, -17.84) * mm, "end": v(-23.43, -13.53) * mm});
            skLineSegment(sketch, "E60.1.11.0", {"start": v(-20.1, -18.1) * mm, "end": v(-23.31, -20.99) * mm});
            skLineSegment(sketch, "E60.3.11.0", {"start": v(-23.31, -20.99) * mm, "end": v(-19.2, -22.32) * mm});
            skLineSegment(sketch, "E60.6.11.0", {"start": v(-19.2, -22.32) * mm, "end": v(-20.1, -18.1) * mm});
            skLineSegment(sketch, "E60.1.12.0", {"start": v(-15.9, -21.88) * mm, "end": v(-18.44, -25.38) * mm});
            skLineSegment(sketch, "E60.3.12.0", {"start": v(-18.44, -25.38) * mm, "end": v(-14.14, -25.83) * mm});
            skLineSegment(sketch, "E60.6.12.0", {"start": v(-14.14, -25.83) * mm, "end": v(-15.9, -21.88) * mm});
            skLineSegment(sketch, "E60.1.13.0", {"start": v(-11, -24.71) * mm, "end": v(-12.76, -28.66) * mm});
            skLineSegment(sketch, "E60.3.13.0", {"start": v(-12.76, -28.66) * mm, "end": v(-8.46, -28.2) * mm});
            skLineSegment(sketch, "E60.6.13.0", {"start": v(-8.46, -28.2) * mm, "end": v(-11, -24.71) * mm});
            skLineSegment(sketch, "E60.1.14.0", {"start": v(-5.62, -26.46) * mm, "end": v(-6.52, -30.68) * mm});
            skLineSegment(sketch, "E60.3.14.0", {"start": v(-6.52, -30.68) * mm, "end": v(-2.42, -29.35) * mm});
            skLineSegment(sketch, "E60.6.14.0", {"start": v(-2.42, -29.35) * mm, "end": v(-5.62, -26.46) * mm});
            skLineSegment(sketch, "E60.1.15.0", {"start": v(0, -27.05) * mm, "end": v(0, -31.37) * mm});
            skLineSegment(sketch, "E60.3.15.0", {"start": v(0, -31.37) * mm, "end": v(3.74, -29.21) * mm});
            skLineSegment(sketch, "E60.6.15.0", {"start": v(3.74, -29.21) * mm, "end": v(0, -27.05) * mm});
            skLineSegment(sketch, "E60.1.16.0", {"start": v(5.62, -26.46) * mm, "end": v(6.52, -30.68) * mm});
            skLineSegment(sketch, "E60.3.16.0", {"start": v(6.52, -30.68) * mm, "end": v(9.73, -27.8) * mm});
            skLineSegment(sketch, "E60.6.16.0", {"start": v(9.73, -27.8) * mm, "end": v(5.62, -26.46) * mm});
            skLineSegment(sketch, "E60.1.17.0", {"start": v(11, -24.71) * mm, "end": v(12.76, -28.66) * mm});
            skLineSegment(sketch, "E60.3.17.0", {"start": v(12.76, -28.66) * mm, "end": v(15.3, -25.16) * mm});
            skLineSegment(sketch, "E60.6.17.0", {"start": v(15.3, -25.16) * mm, "end": v(11, -24.71) * mm});
            skLineSegment(sketch, "E60.1.18.0", {"start": v(15.9, -21.88) * mm, "end": v(18.44, -25.38) * mm});
            skLineSegment(sketch, "E60.3.18.0", {"start": v(18.44, -25.38) * mm, "end": v(20.2, -21.43) * mm});
            skLineSegment(sketch, "E60.6.18.0", {"start": v(20.2, -21.43) * mm, "end": v(15.9, -21.88) * mm});
            skLineSegment(sketch, "E60.1.19.0", {"start": v(20.1, -18.1) * mm, "end": v(23.31, -20.99) * mm});
            skLineSegment(sketch, "E60.3.19.0", {"start": v(23.31, -20.99) * mm, "end": v(24.2, -16.77) * mm});
            skLineSegment(sketch, "E60.6.19.0", {"start": v(24.2, -16.77) * mm, "end": v(20.1, -18.1) * mm});
            skLineSegment(sketch, "E60.1.20.0", {"start": v(23.43, -13.53) * mm, "end": v(27.17, -15.68) * mm});
            skLineSegment(sketch, "E60.3.20.0", {"start": v(27.17, -15.68) * mm, "end": v(27.17, -11.37) * mm});
            skLineSegment(sketch, "E60.6.20.0", {"start": v(27.17, -11.37) * mm, "end": v(23.43, -13.53) * mm});
            skLineSegment(sketch, "E60.1.21.0", {"start": v(25.73, -8.36) * mm, "end": v(29.83, -9.7) * mm});
            skLineSegment(sketch, "E60.3.21.0", {"start": v(29.83, -9.7) * mm, "end": v(28.94, -5.47) * mm});
            skLineSegment(sketch, "E60.6.21.0", {"start": v(28.94, -5.47) * mm, "end": v(25.73, -8.36) * mm});
            skLineSegment(sketch, "E60.1.22.0", {"start": v(26.9, -2.83) * mm, "end": v(31.2, -3.28) * mm});
            skLineSegment(sketch, "E60.3.22.0", {"start": v(31.2, -3.28) * mm, "end": v(29.44, 0.67) * mm});
            skLineSegment(sketch, "E60.6.22.0", {"start": v(29.44, 0.67) * mm, "end": v(26.9, -2.83) * mm});
            skLineSegment(sketch, "E60.1.23.0", {"start": v(26.9, 2.83) * mm, "end": v(31.2, 3.28) * mm});
            skLineSegment(sketch, "E60.3.23.0", {"start": v(31.2, 3.28) * mm, "end": v(28.66, 6.77) * mm});
            skLineSegment(sketch, "E60.6.23.0", {"start": v(28.66, 6.77) * mm, "end": v(26.9, 2.83) * mm});
            skLineSegment(sketch, "E60.1.24.0", {"start": v(25.73, 8.36) * mm, "end": v(29.83, 9.7) * mm});
            skLineSegment(sketch, "E60.3.24.0", {"start": v(29.83, 9.7) * mm, "end": v(26.62, 12.58) * mm});
            skLineSegment(sketch, "E60.6.24.0", {"start": v(26.62, 12.58) * mm, "end": v(25.73, 8.36) * mm});
            skLineSegment(sketch, "E60.1.25.0", {"start": v(23.43, 13.53) * mm, "end": v(27.17, 15.68) * mm});
            skLineSegment(sketch, "E60.3.25.0", {"start": v(27.17, 15.68) * mm, "end": v(23.43, 17.84) * mm});
            skLineSegment(sketch, "E60.6.25.0", {"start": v(23.43, 17.84) * mm, "end": v(23.43, 13.53) * mm});
            skLineSegment(sketch, "E60.1.26.0", {"start": v(20.1, 18.1) * mm, "end": v(23.31, 20.99) * mm});
            skLineSegment(sketch, "E60.3.26.0", {"start": v(23.31, 20.99) * mm, "end": v(19.2, 22.32) * mm});
            skLineSegment(sketch, "E60.6.26.0", {"start": v(19.2, 22.32) * mm, "end": v(20.1, 18.1) * mm});
            skLineSegment(sketch, "E60.1.27.0", {"start": v(15.9, 21.88) * mm, "end": v(18.44, 25.38) * mm});
            skLineSegment(sketch, "E60.3.27.0", {"start": v(18.44, 25.38) * mm, "end": v(14.14, 25.83) * mm});
            skLineSegment(sketch, "E60.6.27.0", {"start": v(14.14, 25.83) * mm, "end": v(15.9, 21.88) * mm});
            skLineSegment(sketch, "E60.1.28.0", {"start": v(11, 24.71) * mm, "end": v(12.76, 28.66) * mm});
            skLineSegment(sketch, "E60.3.28.0", {"start": v(12.76, 28.66) * mm, "end": v(8.46, 28.2) * mm});
            skLineSegment(sketch, "E60.6.28.0", {"start": v(8.46, 28.2) * mm, "end": v(11, 24.71) * mm});
            skLineSegment(sketch, "E60.1.29.0", {"start": v(5.62, 26.46) * mm, "end": v(6.52, 30.68) * mm});
            skLineSegment(sketch, "E60.3.29.0", {"start": v(6.52, 30.68) * mm, "end": v(2.42, 29.35) * mm});
            skLineSegment(sketch, "E60.6.29.0", {"start": v(2.42, 29.35) * mm, "end": v(5.62, 26.46) * mm});
            skLineSegment(sketch, "E61.2.18.0", {"start": v(22.23, -3.74) * mm, "end": v(20.07, 0) * mm});
            skLineSegment(sketch, "E61.3.18.0", {"start": v(20.07, 0) * mm, "end": v(24.38, 0) * mm});
            skLineSegment(sketch, "E61.6.18.0", {"start": v(24.38, 0) * mm, "end": v(22.23, -3.74) * mm});
            skLineSegment(sketch, "E61.2.19.0", {"start": v(22.44, 2.14) * mm, "end": v(19.38, 5.2) * mm});
            skLineSegment(sketch, "E61.3.19.0", {"start": v(19.38, 5.2) * mm, "end": v(23.55, 6.31) * mm});
            skLineSegment(sketch, "E61.6.19.0", {"start": v(23.55, 6.31) * mm, "end": v(22.44, 2.14) * mm});
            skLineSegment(sketch, "E61.2.20.0", {"start": v(21.12, 7.87) * mm, "end": v(17.38, 10.03) * mm});
            skLineSegment(sketch, "E61.3.20.0", {"start": v(17.38, 10.03) * mm, "end": v(21.12, 12.2) * mm});
            skLineSegment(sketch, "E61.6.20.0", {"start": v(21.12, 12.2) * mm, "end": v(21.12, 7.87) * mm});
            skLineSegment(sketch, "E61.2.21.0", {"start": v(18.36, 13.07) * mm, "end": v(14.19, 14.19) * mm});
            skLineSegment(sketch, "E61.3.21.0", {"start": v(14.19, 14.19) * mm, "end": v(17.24, 17.24) * mm});
            skLineSegment(sketch, "E61.6.21.0", {"start": v(17.24, 17.24) * mm, "end": v(18.36, 13.07) * mm});
            skLineSegment(sketch, "E61.2.22.0", {"start": v(14.35, 17.38) * mm, "end": v(10.03, 17.38) * mm});
            skLineSegment(sketch, "E61.3.22.0", {"start": v(10.03, 17.38) * mm, "end": v(12.2, 21.12) * mm});
            skLineSegment(sketch, "E61.6.22.0", {"start": v(12.2, 21.12) * mm, "end": v(14.35, 17.38) * mm});
            skLineSegment(sketch, "E61.2.23.0", {"start": v(9.36, 20.5) * mm, "end": v(5.2, 19.38) * mm});
            skLineSegment(sketch, "E61.3.23.0", {"start": v(5.2, 19.38) * mm, "end": v(6.31, 23.55) * mm});
            skLineSegment(sketch, "E61.6.23.0", {"start": v(6.31, 23.55) * mm, "end": v(9.36, 20.5) * mm});
            skLineSegment(sketch, "E62.2.12.0", {"start": v(17.4, 0) * mm, "end": v(15.24, 3.74) * mm});
            skLineSegment(sketch, "E62.3.12.0", {"start": v(13.08, 0) * mm, "end": v(17.4, 0) * mm});
            skLineSegment(sketch, "E62.6.12.0", {"start": v(15.24, 3.74) * mm, "end": v(13.08, 0) * mm});
            skLineSegment(sketch, "E62.2.13.0", {"start": v(16.07, 6.66) * mm, "end": v(12.65, 9.29) * mm});
            skLineSegment(sketch, "E62.3.13.0", {"start": v(12.09, 5) * mm, "end": v(16.07, 6.66) * mm});
            skLineSegment(sketch, "E62.6.13.0", {"start": v(12.65, 9.29) * mm, "end": v(12.09, 5) * mm});
            skLineSegment(sketch, "E62.2.14.0", {"start": v(12.3, 12.3) * mm, "end": v(8.13, 13.42) * mm});
            skLineSegment(sketch, "E62.3.14.0", {"start": v(9.25, 9.25) * mm, "end": v(12.3, 12.3) * mm});
            skLineSegment(sketch, "E62.6.14.0", {"start": v(8.13, 13.42) * mm, "end": v(9.25, 9.25) * mm});
            skLineSegment(sketch, "E62.2.15.0", {"start": v(6.66, 16.07) * mm, "end": v(2.38, 15.51) * mm});
            skLineSegment(sketch, "E62.3.15.0", {"start": v(5, 12.09) * mm, "end": v(6.66, 16.07) * mm});
            skLineSegment(sketch, "E62.6.15.0", {"start": v(2.38, 15.51) * mm, "end": v(5, 12.09) * mm});
            skLineSegment(sketch, "E63.1.0", {"start": v(-2.97, 36.27) * mm, "end": v(-6.25, 33.46) * mm});
            skLineSegment(sketch, "E63.1.1", {"start": v(-7.05, 37.7) * mm, "end": v(-2.97, 36.27) * mm});
            skLineSegment(sketch, "E63.1.2", {"start": v(-6.25, 33.46) * mm, "end": v(-7.05, 37.7) * mm});
            skLineSegment(sketch, "E63.2.0", {"start": v(-9.59, 35.1) * mm, "end": v(-12.3, 31.74) * mm});
            skLineSegment(sketch, "E63.2.1", {"start": v(-13.86, 35.76) * mm, "end": v(-9.59, 35.1) * mm});
            skLineSegment(sketch, "E63.2.2", {"start": v(-12.3, 31.74) * mm, "end": v(-13.86, 35.76) * mm});
            skLineSegment(sketch, "E64.2.3.0", {"start": v(-15.87, 32.74) * mm, "end": v(-17.92, 28.94) * mm});
            skLineSegment(sketch, "E64.3.3.0", {"start": v(-20.2, 32.6) * mm, "end": v(-15.87, 32.74) * mm});
            skLineSegment(sketch, "E64.6.3.0", {"start": v(-17.92, 28.94) * mm, "end": v(-20.2, 32.6) * mm});
            skLineSegment(sketch, "E64.2.4.0", {"start": v(-21.62, 29.27) * mm, "end": v(-22.93, 25.15) * mm});
            skLineSegment(sketch, "E64.3.4.0", {"start": v(-25.84, 28.34) * mm, "end": v(-21.62, 29.27) * mm});
            skLineSegment(sketch, "E64.6.4.0", {"start": v(-22.93, 25.15) * mm, "end": v(-25.84, 28.34) * mm});
            skLineSegment(sketch, "E64.2.5.0", {"start": v(-26.63, 24.8) * mm, "end": v(-27.16, 20.51) * mm});
            skLineSegment(sketch, "E64.3.5.0", {"start": v(-30.6, 23.11) * mm, "end": v(-26.63, 24.8) * mm});
            skLineSegment(sketch, "E64.6.5.0", {"start": v(-27.16, 20.51) * mm, "end": v(-30.6, 23.11) * mm});
            skLineSegment(sketch, "E64.2.6.0", {"start": v(-30.73, 19.48) * mm, "end": v(-30.47, 15.17) * mm});
            skLineSegment(sketch, "E64.3.6.0", {"start": v(-34.33, 17.1) * mm, "end": v(-30.73, 19.48) * mm});
            skLineSegment(sketch, "E64.6.6.0", {"start": v(-30.47, 15.17) * mm, "end": v(-34.33, 17.1) * mm});
            skLineSegment(sketch, "E64.2.7.0", {"start": v(-33.79, 13.5) * mm, "end": v(-32.74, 9.31) * mm});
            skLineSegment(sketch, "E64.3.7.0", {"start": v(-36.89, 10.5) * mm, "end": v(-33.79, 13.5) * mm});
            skLineSegment(sketch, "E64.6.7.0", {"start": v(-32.74, 9.31) * mm, "end": v(-36.89, 10.5) * mm});
            skLineSegment(sketch, "E64.2.8.0", {"start": v(-35.7, 7.06) * mm, "end": v(-33.9, 3.14) * mm});
            skLineSegment(sketch, "E64.3.8.0", {"start": v(-38.2, 3.54) * mm, "end": v(-35.7, 7.06) * mm});
            skLineSegment(sketch, "E64.6.8.0", {"start": v(-33.9, 3.14) * mm, "end": v(-38.2, 3.54) * mm});
            skLineSegment(sketch, "E64.2.9.0", {"start": v(-36.39, 0.38) * mm, "end": v(-33.9, -3.14) * mm});
            skLineSegment(sketch, "E64.3.9.0", {"start": v(-38.2, -3.54) * mm, "end": v(-36.39, 0.38) * mm});
            skLineSegment(sketch, "E64.6.9.0", {"start": v(-33.9, -3.14) * mm, "end": v(-38.2, -3.54) * mm});
            skLineSegment(sketch, "E64.2.10.0", {"start": v(-35.84, -6.3) * mm, "end": v(-32.74, -9.31) * mm});
            skLineSegment(sketch, "E64.3.10.0", {"start": v(-36.89, -10.5) * mm, "end": v(-35.84, -6.3) * mm});
            skLineSegment(sketch, "E64.6.10.0", {"start": v(-32.74, -9.31) * mm, "end": v(-36.89, -10.5) * mm});
            skLineSegment(sketch, "E64.2.11.0", {"start": v(-34.07, -12.79) * mm, "end": v(-30.47, -15.17) * mm});
            skLineSegment(sketch, "E64.3.11.0", {"start": v(-34.33, -17.1) * mm, "end": v(-34.07, -12.79) * mm});
            skLineSegment(sketch, "E64.6.11.0", {"start": v(-30.47, -15.17) * mm, "end": v(-34.33, -17.1) * mm});
            skLineSegment(sketch, "E64.2.12.0", {"start": v(-31.14, -18.83) * mm, "end": v(-27.16, -20.51) * mm});
            skLineSegment(sketch, "E64.3.12.0", {"start": v(-30.6, -23.11) * mm, "end": v(-31.14, -18.83) * mm});
            skLineSegment(sketch, "E64.6.12.0", {"start": v(-27.16, -20.51) * mm, "end": v(-30.6, -23.11) * mm});
            skLineSegment(sketch, "E64.2.13.0", {"start": v(-27.15, -24.23) * mm, "end": v(-22.93, -25.15) * mm});
            skLineSegment(sketch, "E64.3.13.0", {"start": v(-25.84, -28.34) * mm, "end": v(-27.15, -24.23) * mm});
            skLineSegment(sketch, "E64.6.13.0", {"start": v(-22.93, -25.15) * mm, "end": v(-25.84, -28.34) * mm});
            skLineSegment(sketch, "E64.2.14.0", {"start": v(-22.23, -28.8) * mm, "end": v(-17.92, -28.94) * mm});
            skLineSegment(sketch, "E64.3.14.0", {"start": v(-20.2, -32.6) * mm, "end": v(-22.23, -28.8) * mm});
            skLineSegment(sketch, "E64.6.14.0", {"start": v(-17.92, -28.94) * mm, "end": v(-20.2, -32.6) * mm});
            skLineSegment(sketch, "E64.2.15.0", {"start": v(-16.56, -32.4) * mm, "end": v(-12.3, -31.74) * mm});
            skLineSegment(sketch, "E64.3.15.0", {"start": v(-13.86, -35.76) * mm, "end": v(-16.56, -32.4) * mm});
            skLineSegment(sketch, "E64.6.15.0", {"start": v(-12.3, -31.74) * mm, "end": v(-13.86, -35.76) * mm});
            skLineSegment(sketch, "E64.2.16.0", {"start": v(-10.33, -34.9) * mm, "end": v(-6.25, -33.46) * mm});
            skLineSegment(sketch, "E64.3.16.0", {"start": v(-7.05, -37.7) * mm, "end": v(-10.33, -34.9) * mm});
            skLineSegment(sketch, "E64.6.16.0", {"start": v(-6.25, -33.46) * mm, "end": v(-7.05, -37.7) * mm});
            skLineSegment(sketch, "E64.2.17.0", {"start": v(-3.74, -36.2) * mm, "end": v(0, -34.04) * mm});
            skLineSegment(sketch, "E64.3.17.0", {"start": v(0, -38.35) * mm, "end": v(-3.74, -36.2) * mm});
            skLineSegment(sketch, "E64.6.17.0", {"start": v(0, -34.04) * mm, "end": v(0, -38.35) * mm});
            skLineSegment(sketch, "E64.2.18.0", {"start": v(2.97, -36.27) * mm, "end": v(6.25, -33.46) * mm});
            skLineSegment(sketch, "E64.3.18.0", {"start": v(7.05, -37.7) * mm, "end": v(2.97, -36.27) * mm});
            skLineSegment(sketch, "E64.6.18.0", {"start": v(6.25, -33.46) * mm, "end": v(7.05, -37.7) * mm});
            skLineSegment(sketch, "E64.2.19.0", {"start": v(9.59, -35.1) * mm, "end": v(12.3, -31.74) * mm});
            skLineSegment(sketch, "E64.3.19.0", {"start": v(13.86, -35.76) * mm, "end": v(9.59, -35.1) * mm});
            skLineSegment(sketch, "E64.6.19.0", {"start": v(12.3, -31.74) * mm, "end": v(13.86, -35.76) * mm});
            skLineSegment(sketch, "E64.2.20.0", {"start": v(15.87, -32.74) * mm, "end": v(17.92, -28.94) * mm});
            skLineSegment(sketch, "E64.3.20.0", {"start": v(20.2, -32.6) * mm, "end": v(15.87, -32.74) * mm});
            skLineSegment(sketch, "E64.6.20.0", {"start": v(17.92, -28.94) * mm, "end": v(20.2, -32.6) * mm});
            skLineSegment(sketch, "E64.2.21.0", {"start": v(21.62, -29.27) * mm, "end": v(22.93, -25.15) * mm});
            skLineSegment(sketch, "E64.3.21.0", {"start": v(25.84, -28.34) * mm, "end": v(21.62, -29.27) * mm});
            skLineSegment(sketch, "E64.6.21.0", {"start": v(22.93, -25.15) * mm, "end": v(25.84, -28.34) * mm});
            skLineSegment(sketch, "E64.2.22.0", {"start": v(26.63, -24.8) * mm, "end": v(27.16, -20.51) * mm});
            skLineSegment(sketch, "E64.3.22.0", {"start": v(30.6, -23.11) * mm, "end": v(26.63, -24.8) * mm});
            skLineSegment(sketch, "E64.6.22.0", {"start": v(27.16, -20.51) * mm, "end": v(30.6, -23.11) * mm});
            skLineSegment(sketch, "E64.2.23.0", {"start": v(30.73, -19.48) * mm, "end": v(30.47, -15.17) * mm});
            skLineSegment(sketch, "E64.3.23.0", {"start": v(34.33, -17.1) * mm, "end": v(30.73, -19.48) * mm});
            skLineSegment(sketch, "E64.6.23.0", {"start": v(30.47, -15.17) * mm, "end": v(34.33, -17.1) * mm});
            skLineSegment(sketch, "E64.2.24.0", {"start": v(33.79, -13.5) * mm, "end": v(32.74, -9.31) * mm});
            skLineSegment(sketch, "E64.3.24.0", {"start": v(36.89, -10.5) * mm, "end": v(33.79, -13.5) * mm});
            skLineSegment(sketch, "E64.6.24.0", {"start": v(32.74, -9.31) * mm, "end": v(36.89, -10.5) * mm});
            skLineSegment(sketch, "E64.2.25.0", {"start": v(35.7, -7.06) * mm, "end": v(33.9, -3.14) * mm});
            skLineSegment(sketch, "E64.3.25.0", {"start": v(38.2, -3.54) * mm, "end": v(35.7, -7.06) * mm});
            skLineSegment(sketch, "E64.6.25.0", {"start": v(33.9, -3.14) * mm, "end": v(38.2, -3.54) * mm});
            skLineSegment(sketch, "E64.2.26.0", {"start": v(36.39, -0.38) * mm, "end": v(33.9, 3.14) * mm});
            skLineSegment(sketch, "E64.3.26.0", {"start": v(38.2, 3.54) * mm, "end": v(36.39, -0.38) * mm});
            skLineSegment(sketch, "E64.6.26.0", {"start": v(33.9, 3.14) * mm, "end": v(38.2, 3.54) * mm});
            skLineSegment(sketch, "E64.2.27.0", {"start": v(35.84, 6.3) * mm, "end": v(32.74, 9.31) * mm});
            skLineSegment(sketch, "E64.3.27.0", {"start": v(36.89, 10.5) * mm, "end": v(35.84, 6.3) * mm});
            skLineSegment(sketch, "E64.6.27.0", {"start": v(32.74, 9.31) * mm, "end": v(36.89, 10.5) * mm});
            skLineSegment(sketch, "E64.2.28.0", {"start": v(34.07, 12.79) * mm, "end": v(30.47, 15.17) * mm});
            skLineSegment(sketch, "E64.3.28.0", {"start": v(34.33, 17.1) * mm, "end": v(34.07, 12.79) * mm});
            skLineSegment(sketch, "E64.6.28.0", {"start": v(30.47, 15.17) * mm, "end": v(34.33, 17.1) * mm});
            skLineSegment(sketch, "E64.2.29.0", {"start": v(31.14, 18.83) * mm, "end": v(27.16, 20.51) * mm});
            skLineSegment(sketch, "E64.3.29.0", {"start": v(30.6, 23.11) * mm, "end": v(31.14, 18.83) * mm});
            skLineSegment(sketch, "E64.6.29.0", {"start": v(27.16, 20.51) * mm, "end": v(30.6, 23.11) * mm});
            skLineSegment(sketch, "E64.2.30.0", {"start": v(27.15, 24.23) * mm, "end": v(22.93, 25.15) * mm});
            skLineSegment(sketch, "E64.3.30.0", {"start": v(25.84, 28.34) * mm, "end": v(27.15, 24.23) * mm});
            skLineSegment(sketch, "E64.6.30.0", {"start": v(22.93, 25.15) * mm, "end": v(25.84, 28.34) * mm});
            skLineSegment(sketch, "E64.2.31.0", {"start": v(22.23, 28.8) * mm, "end": v(17.92, 28.94) * mm});
            skLineSegment(sketch, "E64.3.31.0", {"start": v(20.2, 32.6) * mm, "end": v(22.23, 28.8) * mm});
            skLineSegment(sketch, "E64.6.31.0", {"start": v(17.92, 28.94) * mm, "end": v(20.2, 32.6) * mm});
            skLineSegment(sketch, "E64.2.32.0", {"start": v(16.56, 32.4) * mm, "end": v(12.3, 31.74) * mm});
            skLineSegment(sketch, "E64.3.32.0", {"start": v(13.86, 35.76) * mm, "end": v(16.56, 32.4) * mm});
            skLineSegment(sketch, "E64.6.32.0", {"start": v(12.3, 31.74) * mm, "end": v(13.86, 35.76) * mm});
            skLineSegment(sketch, "E64.2.33.0", {"start": v(10.33, 34.9) * mm, "end": v(6.25, 33.46) * mm});
            skLineSegment(sketch, "E64.3.33.0", {"start": v(7.05, 37.7) * mm, "end": v(10.33, 34.9) * mm});
            skLineSegment(sketch, "E64.6.33.0", {"start": v(6.25, 33.46) * mm, "end": v(7.05, 37.7) * mm});
            skSolve(sketch);
        }
        {
            var Q0;
            Q0=makeQuery(id+"F28.imprint","IMPRINT",FACE,{"disambiguationData":[TD([[makeQuery(id+"F28.imprint","IMPRINT",EDGE,{"derivedFrom":sQuery(id+"F28.wireOp",EDGE,"E55.1.0")}),1.0]])]});
            var Q1;
            Q1=makeQuery(id+"F28.imprint","IMPRINT",FACE,{"disambiguationData":[TD([[makeQuery(id+"F28.imprint","IMPRINT",EDGE,{"derivedFrom":sQuery(id+"F28.wireOp",EDGE,"E55.2.0")}),1.0]])]});
            var Q2;
            Q2=makeQuery(id+"F28.imprint","IMPRINT",FACE,{"disambiguationData":[TD([[makeQuery(id+"F28.imprint","IMPRINT",EDGE,{"derivedFrom":sQuery(id+"F28.wireOp",EDGE,"E62.2.15.0")}),1.0]])]});
            var Q3;
            Q3=makeQuery(id+"F28.imprint","IMPRINT",FACE,{"disambiguationData":[TD([[makeQuery(id+"F28.imprint","IMPRINT",EDGE,{"derivedFrom":sQuery(id+"F28.wireOp",EDGE,"E62.2.14.0")}),1.0]])]});
            var Q4;
            Q4=makeQuery(id+"F28.imprint","IMPRINT",FACE,{"disambiguationData":[TD([[makeQuery(id+"F28.imprint","IMPRINT",EDGE,{"derivedFrom":sQuery(id+"F28.wireOp",EDGE,"E56.2.11.0")}),1.0]])]});
            var Q5;
            Q5=makeQuery(id+"F28.imprint","IMPRINT",FACE,{"disambiguationData":[TD([[makeQuery(id+"F28.imprint","IMPRINT",EDGE,{"derivedFrom":sQuery(id+"F28.wireOp",EDGE,"E62.2.13.0")}),1.0]])]});
            var Q6;
            Q6=makeQuery(id+"F28.imprint","IMPRINT",FACE,{"disambiguationData":[TD([[makeQuery(id+"F28.imprint","IMPRINT",EDGE,{"derivedFrom":sQuery(id+"F28.wireOp",EDGE,"E62.2.12.0")}),1.0]])]});
            var Q7;
            Q7=makeQuery(id+"F28.imprint","IMPRINT",FACE,{"disambiguationData":[TD([[makeQuery(id+"F28.imprint","IMPRINT",EDGE,{"derivedFrom":sQuery(id+"F28.wireOp",EDGE,"E56.2.10.0")}),1.0]])]});
            var Q8;
            Q8=makeQuery(id+"F28.imprint","IMPRINT",FACE,{"disambiguationData":[TD([[makeQuery(id+"F28.imprint","IMPRINT",EDGE,{"derivedFrom":sQuery(id+"F28.wireOp",EDGE,"E56.2.9.0")}),1.0]])]});
            var Q9;
            Q9=makeQuery(id+"F28.imprint","IMPRINT",FACE,{"disambiguationData":[TD([[makeQuery(id+"F28.imprint","IMPRINT",EDGE,{"derivedFrom":sQuery(id+"F28.wireOp",EDGE,"E56.2.8.0")}),1.0]])]});
            var Q10;
            Q10=makeQuery(id+"F28.imprint","IMPRINT",FACE,{"disambiguationData":[TD([[makeQuery(id+"F28.imprint","IMPRINT",EDGE,{"derivedFrom":sQuery(id+"F28.wireOp",EDGE,"E56.2.7.0")}),1.0]])]});
            var Q11;
            Q11=makeQuery(id+"F28.imprint","IMPRINT",FACE,{"disambiguationData":[TD([[makeQuery(id+"F28.imprint","IMPRINT",EDGE,{"derivedFrom":sQuery(id+"F28.wireOp",EDGE,"E56.2.6.0")}),1.0]])]});
            var Q12;
            Q12=makeQuery(id+"F28.imprint","IMPRINT",FACE,{"disambiguationData":[TD([[makeQuery(id+"F28.imprint","IMPRINT",EDGE,{"derivedFrom":sQuery(id+"F28.wireOp",EDGE,"E56.2.5.0")}),1.0]])]});
            var Q13;
            Q13=makeQuery(id+"F28.imprint","IMPRINT",FACE,{"disambiguationData":[TD([[makeQuery(id+"F28.imprint","IMPRINT",EDGE,{"derivedFrom":sQuery(id+"F28.wireOp",EDGE,"E56.2.4.0")}),1.0]])]});
            var Q14;
            Q14=makeQuery(id+"F28.imprint","IMPRINT",FACE,{"disambiguationData":[TD([[makeQuery(id+"F28.imprint","IMPRINT",EDGE,{"derivedFrom":sQuery(id+"F28.wireOp",EDGE,"E56.2.3.0")}),1.0]])]});
            var Q15;
            Q15=makeQuery(id+"F28.imprint","IMPRINT",FACE,{"disambiguationData":[TD([[makeQuery(id+"F28.imprint","IMPRINT",EDGE,{"derivedFrom":sQuery(id+"F28.wireOp",EDGE,"E43")}),1.0]])]});
            extrude(context, id + "F29", {"entities" : qUnion([Q0, Q1, Q2, Q3, Q4, Q5, Q6, Q7, Q8, Q9, Q10, Q11, Q12, Q13, Q14, Q15]), "operationType" : NewBodyOperationType.ADD, "depth" : 5.84 * mm});
        }
        {
            var Q0;
            Q0=makeQuery(id+"F28.imprint","IMPRINT",FACE,{"disambiguationData":[TD([[makeQuery(id+"F28.imprint","IMPRINT",EDGE,{"derivedFrom":sQuery(id+"F28.wireOp",EDGE,"E58.2.5.0")}),-1.0]])]});
            var Q1;
            Q1=makeQuery(id+"F28.imprint","IMPRINT",FACE,{"disambiguationData":[TD([[makeQuery(id+"F28.imprint","IMPRINT",EDGE,{"derivedFrom":sQuery(id+"F28.wireOp",EDGE,"E58.2.4.0")}),-1.0]])]});
            var Q2;
            Q2=makeQuery(id+"F28.imprint","IMPRINT",FACE,{"disambiguationData":[TD([[makeQuery(id+"F28.imprint","IMPRINT",EDGE,{"derivedFrom":sQuery(id+"F28.wireOp",EDGE,"E58.2.3.0")}),-1.0]])]});
            var Q3;
            Q3=makeQuery(id+"F28.imprint","IMPRINT",FACE,{"disambiguationData":[TD([[makeQuery(id+"F28.imprint","IMPRINT",EDGE,{"derivedFrom":sQuery(id+"F28.wireOp",EDGE,"E58.2.6.0")}),-1.0]])]});
            var Q4;
            Q4=makeQuery(id+"F28.imprint","IMPRINT",FACE,{"disambiguationData":[TD([[makeQuery(id+"F28.imprint","IMPRINT",EDGE,{"derivedFrom":sQuery(id+"F28.wireOp",EDGE,"E58.2.7.0")}),-1.0]])]});
            var Q5;
            Q5=makeQuery(id+"F28.imprint","IMPRINT",FACE,{"disambiguationData":[TD([[makeQuery(id+"F28.imprint","IMPRINT",EDGE,{"derivedFrom":sQuery(id+"F28.wireOp",EDGE,"E58.2.8.0")}),-1.0]])]});
            var Q6;
            Q6=makeQuery(id+"F28.imprint","IMPRINT",FACE,{"disambiguationData":[TD([[makeQuery(id+"F28.imprint","IMPRINT",EDGE,{"derivedFrom":sQuery(id+"F28.wireOp",EDGE,"E58.2.9.0")}),-1.0]])]});
            var Q7;
            Q7=makeQuery(id+"F28.imprint","IMPRINT",FACE,{"disambiguationData":[TD([[makeQuery(id+"F28.imprint","IMPRINT",EDGE,{"derivedFrom":sQuery(id+"F28.wireOp",EDGE,"E58.2.10.0")}),-1.0]])]});
            var Q8;
            Q8=makeQuery(id+"F28.imprint","IMPRINT",FACE,{"disambiguationData":[TD([[makeQuery(id+"F28.imprint","IMPRINT",EDGE,{"derivedFrom":sQuery(id+"F28.wireOp",EDGE,"E58.2.11.0")}),-1.0]])]});
            var Q9;
            Q9=makeQuery(id+"F28.imprint","IMPRINT",FACE,{"disambiguationData":[TD([[makeQuery(id+"F28.imprint","IMPRINT",EDGE,{"derivedFrom":sQuery(id+"F28.wireOp",EDGE,"E57.2.0")}),-1.0]])]});
            var Q10;
            Q10=makeQuery(id+"F28.imprint","IMPRINT",FACE,{"disambiguationData":[TD([[makeQuery(id+"F28.imprint","IMPRINT",EDGE,{"derivedFrom":sQuery(id+"F28.wireOp",EDGE,"E57.1.0")}),-1.0]])]});
            var Q11;
            Q11=makeQuery(id+"F28.imprint","IMPRINT",FACE,{"disambiguationData":[TD([[makeQuery(id+"F28.imprint","IMPRINT",EDGE,{"derivedFrom":sQuery(id+"F28.wireOp",EDGE,"E46")}),-1.0]])]});
            var Q12;
            Q12=makeQuery(id+"F28.imprint","IMPRINT",FACE,{"disambiguationData":[TD([[makeQuery(id+"F28.imprint","IMPRINT",EDGE,{"derivedFrom":sQuery(id+"F28.wireOp",EDGE,"E61.2.23.0")}),-1.0]])]});
            var Q13;
            Q13=makeQuery(id+"F28.imprint","IMPRINT",FACE,{"disambiguationData":[TD([[makeQuery(id+"F28.imprint","IMPRINT",EDGE,{"derivedFrom":sQuery(id+"F28.wireOp",EDGE,"E61.2.22.0")}),-1.0]])]});
            var Q14;
            Q14=makeQuery(id+"F28.imprint","IMPRINT",FACE,{"disambiguationData":[TD([[makeQuery(id+"F28.imprint","IMPRINT",EDGE,{"derivedFrom":sQuery(id+"F28.wireOp",EDGE,"E61.2.21.0")}),-1.0]])]});
            var Q15;
            Q15=makeQuery(id+"F28.imprint","IMPRINT",FACE,{"disambiguationData":[TD([[makeQuery(id+"F28.imprint","IMPRINT",EDGE,{"derivedFrom":sQuery(id+"F28.wireOp",EDGE,"E61.2.20.0")}),-1.0]])]});
            var Q16;
            Q16=makeQuery(id+"F28.imprint","IMPRINT",FACE,{"disambiguationData":[TD([[makeQuery(id+"F28.imprint","IMPRINT",EDGE,{"derivedFrom":sQuery(id+"F28.wireOp",EDGE,"E61.2.19.0")}),-1.0]])]});
            var Q17;
            Q17=makeQuery(id+"F28.imprint","IMPRINT",FACE,{"disambiguationData":[TD([[makeQuery(id+"F28.imprint","IMPRINT",EDGE,{"derivedFrom":sQuery(id+"F28.wireOp",EDGE,"E61.2.18.0")}),-1.0]])]});
            var Q18;
            Q18=makeQuery(id+"F28.imprint","IMPRINT",FACE,{"disambiguationData":[TD([[makeQuery(id+"F28.imprint","IMPRINT",EDGE,{"derivedFrom":sQuery(id+"F28.wireOp",EDGE,"E58.2.17.0")}),-1.0]])]});
            var Q19;
            Q19=makeQuery(id+"F28.imprint","IMPRINT",FACE,{"disambiguationData":[TD([[makeQuery(id+"F28.imprint","IMPRINT",EDGE,{"derivedFrom":sQuery(id+"F28.wireOp",EDGE,"E58.2.16.0")}),-1.0]])]});
            var Q20;
            Q20=makeQuery(id+"F28.imprint","IMPRINT",FACE,{"disambiguationData":[TD([[makeQuery(id+"F28.imprint","IMPRINT",EDGE,{"derivedFrom":sQuery(id+"F28.wireOp",EDGE,"E58.2.15.0")}),-1.0]])]});
            var Q21;
            Q21=makeQuery(id+"F28.imprint","IMPRINT",FACE,{"disambiguationData":[TD([[makeQuery(id+"F28.imprint","IMPRINT",EDGE,{"derivedFrom":sQuery(id+"F28.wireOp",EDGE,"E58.2.14.0")}),-1.0]])]});
            var Q22;
            Q22=makeQuery(id+"F28.imprint","IMPRINT",FACE,{"disambiguationData":[TD([[makeQuery(id+"F28.imprint","IMPRINT",EDGE,{"derivedFrom":sQuery(id+"F28.wireOp",EDGE,"E58.2.13.0")}),-1.0]])]});
            var Q23;
            Q23=makeQuery(id+"F28.imprint","IMPRINT",FACE,{"disambiguationData":[TD([[makeQuery(id+"F28.imprint","IMPRINT",EDGE,{"derivedFrom":sQuery(id+"F28.wireOp",EDGE,"E58.2.12.0")}),-1.0]])]});
            extrude(context, id + "F30", {"entities" : qUnion([Q0, Q1, Q2, Q3, Q4, Q5, Q6, Q7, Q8, Q9, Q10, Q11, Q12, Q13, Q14, Q15, Q16, Q17, Q18, Q19, Q20, Q21, Q22, Q23]), "operationType" : NewBodyOperationType.ADD, "depth" : 12.2 * mm});
        }
        {
            var Q0;
            {var subQ0=sQuery(id+"F28.wireOp",EDGE,"E60.6.27.0");var subQ1=sQuery(id+"F28.wireOp",EDGE,"E60.1.27.0");var subQ2=makeQuery(id+"F28.imprint","INTERSECT",VERTEX,{"derivedFrom":[subQ1,subQ0]});Q0=makeQuery(id+"F28.imprint","IMPRINT",FACE,{"disambiguationData":[TD([[makeQuery(id+"F28.imprint","IMPRINT",EDGE,{"disambiguationData":[TD([[subQ2,-1.0]])],"derivedFrom":subQ1}),1.0]])]});}
            var Q1;
            Q1=makeQuery(id+"F28.imprint","IMPRINT",FACE,{"disambiguationData":[TD([[makeQuery(id+"F28.imprint","IMPRINT",EDGE,{"derivedFrom":sQuery(id+"F28.wireOp",EDGE,"E60.1.26.0")}),1.0]])]});
            var Q2;
            Q2=makeQuery(id+"F28.imprint","IMPRINT",FACE,{"disambiguationData":[TD([[makeQuery(id+"F28.imprint","IMPRINT",EDGE,{"derivedFrom":sQuery(id+"F28.wireOp",EDGE,"E60.1.25.0")}),1.0]])]});
            var Q3;
            Q3=makeQuery(id+"F28.imprint","IMPRINT",FACE,{"disambiguationData":[TD([[makeQuery(id+"F28.imprint","IMPRINT",EDGE,{"derivedFrom":sQuery(id+"F28.wireOp",EDGE,"E60.1.24.0")}),1.0]])]});
            var Q4;
            Q4=makeQuery(id+"F28.imprint","IMPRINT",FACE,{"disambiguationData":[TD([[makeQuery(id+"F28.imprint","IMPRINT",EDGE,{"derivedFrom":sQuery(id+"F28.wireOp",EDGE,"E60.1.23.0")}),1.0]])]});
            var Q5;
            Q5=makeQuery(id+"F28.imprint","IMPRINT",FACE,{"disambiguationData":[TD([[makeQuery(id+"F28.imprint","IMPRINT",EDGE,{"derivedFrom":sQuery(id+"F28.wireOp",EDGE,"E60.1.22.0")}),1.0]])]});
            var Q6;
            Q6=makeQuery(id+"F28.imprint","IMPRINT",FACE,{"disambiguationData":[TD([[makeQuery(id+"F28.imprint","IMPRINT",EDGE,{"derivedFrom":sQuery(id+"F28.wireOp",EDGE,"E60.1.21.0")}),1.0]])]});
            var Q7;
            Q7=makeQuery(id+"F28.imprint","IMPRINT",FACE,{"disambiguationData":[TD([[makeQuery(id+"F28.imprint","IMPRINT",EDGE,{"derivedFrom":sQuery(id+"F28.wireOp",EDGE,"E60.1.20.0")}),1.0]])]});
            var Q8;
            Q8=makeQuery(id+"F28.imprint","IMPRINT",FACE,{"disambiguationData":[TD([[makeQuery(id+"F28.imprint","IMPRINT",EDGE,{"derivedFrom":sQuery(id+"F28.wireOp",EDGE,"E60.1.19.0")}),1.0]])]});
            var Q9;
            {var subQ0=sQuery(id+"F28.wireOp",EDGE,"E60.6.18.0");Q9=makeQuery(id+"F28.imprint","IMPRINT",FACE,{"disambiguationData":[TD([[makeQuery(id+"F28.imprint","IMPRINT",EDGE,{"derivedFrom":subQ0}),1.0]])]});}
            var Q10;
            {var subQ0=sQuery(id+"F28.wireOp",EDGE,"E60.6.12.0");var subQ1=sQuery(id+"F28.wireOp",EDGE,"E60.1.12.0");var subQ2=makeQuery(id+"F28.imprint","INTERSECT",VERTEX,{"derivedFrom":[subQ1,subQ0]});Q10=makeQuery(id+"F28.imprint","IMPRINT",FACE,{"disambiguationData":[TD([[makeQuery(id+"F28.imprint","IMPRINT",EDGE,{"disambiguationData":[TD([[subQ2,-1.0]])],"derivedFrom":subQ1}),1.0]])]});}
            var Q11;
            Q11=makeQuery(id+"F28.imprint","IMPRINT",FACE,{"disambiguationData":[TD([[makeQuery(id+"F28.imprint","IMPRINT",EDGE,{"derivedFrom":sQuery(id+"F28.wireOp",EDGE,"E60.1.11.0")}),1.0]])]});
            var Q12;
            Q12=makeQuery(id+"F28.imprint","IMPRINT",FACE,{"disambiguationData":[TD([[makeQuery(id+"F28.imprint","IMPRINT",EDGE,{"derivedFrom":sQuery(id+"F28.wireOp",EDGE,"E60.1.10.0")}),1.0]])]});
            var Q13;
            Q13=makeQuery(id+"F28.imprint","IMPRINT",FACE,{"disambiguationData":[TD([[makeQuery(id+"F28.imprint","IMPRINT",EDGE,{"derivedFrom":sQuery(id+"F28.wireOp",EDGE,"E60.1.9.0")}),1.0]])]});
            var Q14;
            Q14=makeQuery(id+"F28.imprint","IMPRINT",FACE,{"disambiguationData":[TD([[makeQuery(id+"F28.imprint","IMPRINT",EDGE,{"derivedFrom":sQuery(id+"F28.wireOp",EDGE,"E60.1.8.0")}),1.0]])]});
            var Q15;
            Q15=makeQuery(id+"F28.imprint","IMPRINT",FACE,{"disambiguationData":[TD([[makeQuery(id+"F28.imprint","IMPRINT",EDGE,{"derivedFrom":sQuery(id+"F28.wireOp",EDGE,"E60.1.7.0")}),1.0]])]});
            var Q16;
            Q16=makeQuery(id+"F28.imprint","IMPRINT",FACE,{"disambiguationData":[TD([[makeQuery(id+"F28.imprint","IMPRINT",EDGE,{"derivedFrom":sQuery(id+"F28.wireOp",EDGE,"E60.1.6.0")}),1.0]])]});
            var Q17;
            Q17=makeQuery(id+"F28.imprint","IMPRINT",FACE,{"disambiguationData":[TD([[makeQuery(id+"F28.imprint","IMPRINT",EDGE,{"derivedFrom":sQuery(id+"F28.wireOp",EDGE,"E60.1.5.0")}),1.0]])]});
            var Q18;
            Q18=makeQuery(id+"F28.imprint","IMPRINT",FACE,{"disambiguationData":[TD([[makeQuery(id+"F28.imprint","IMPRINT",EDGE,{"derivedFrom":sQuery(id+"F28.wireOp",EDGE,"E60.1.4.0")}),1.0]])]});
            var Q19;
            {var subQ0=sQuery(id+"F28.wireOp",EDGE,"E60.6.3.0");Q19=makeQuery(id+"F28.imprint","IMPRINT",FACE,{"disambiguationData":[TD([[makeQuery(id+"F28.imprint","IMPRINT",EDGE,{"derivedFrom":subQ0}),1.0]])]});}
            extrude(context, id + "F31", {"entities" : qUnion([Q0, Q1, Q2, Q3, Q4, Q5, Q6, Q7, Q8, Q9, Q10, Q11, Q12, Q13, Q14, Q15, Q16, Q17, Q18, Q19]), "operationType" : NewBodyOperationType.ADD, "depth" : 18.54 * mm});
        }
        {
            var Q0;
            Q0=makeQuery(id+"F28.imprint","IMPRINT",FACE,{"disambiguationData":[TD([[makeQuery(id+"F28.imprint","IMPRINT",EDGE,{"derivedFrom":sQuery(id+"F28.wireOp",EDGE,"E64.2.5.0")}),-1.0]])]});
            var Q1;
            Q1=makeQuery(id+"F28.imprint","IMPRINT",FACE,{"disambiguationData":[TD([[makeQuery(id+"F28.imprint","IMPRINT",EDGE,{"derivedFrom":sQuery(id+"F28.wireOp",EDGE,"E64.2.6.0")}),-1.0]])]});
            var Q2;
            Q2=makeQuery(id+"F28.imprint","IMPRINT",FACE,{"disambiguationData":[TD([[makeQuery(id+"F28.imprint","IMPRINT",EDGE,{"derivedFrom":sQuery(id+"F28.wireOp",EDGE,"E64.2.7.0")}),-1.0]])]});
            var Q3;
            {var subQ0=sQuery(id+"F28.wireOp",EDGE,"E64.2.8.0");Q3=makeQuery(id+"F28.imprint","IMPRINT",FACE,{"disambiguationData":[TD([[makeQuery(id+"F28.imprint","IMPRINT",EDGE,{"derivedFrom":subQ0}),-1.0]])]});}
            var Q4;
            {var subQ0=sQuery(id+"F28.wireOp",EDGE,"E64.2.9.0");Q4=makeQuery(id+"F28.imprint","IMPRINT",FACE,{"disambiguationData":[TD([[makeQuery(id+"F28.imprint","IMPRINT",EDGE,{"derivedFrom":subQ0}),-1.0]])]});}
            var Q5;
            Q5=makeQuery(id+"F28.imprint","IMPRINT",FACE,{"disambiguationData":[TD([[makeQuery(id+"F28.imprint","IMPRINT",EDGE,{"derivedFrom":sQuery(id+"F28.wireOp",EDGE,"E64.2.10.0")}),-1.0]])]});
            var Q6;
            Q6=makeQuery(id+"F28.imprint","IMPRINT",FACE,{"disambiguationData":[TD([[makeQuery(id+"F28.imprint","IMPRINT",EDGE,{"derivedFrom":sQuery(id+"F28.wireOp",EDGE,"E64.2.11.0")}),-1.0]])]});
            var Q7;
            Q7=makeQuery(id+"F28.imprint","IMPRINT",FACE,{"disambiguationData":[TD([[makeQuery(id+"F28.imprint","IMPRINT",EDGE,{"derivedFrom":sQuery(id+"F28.wireOp",EDGE,"E64.2.12.0")}),-1.0]])]});
            var Q8;
            Q8=makeQuery(id+"F28.imprint","IMPRINT",FACE,{"disambiguationData":[TD([[makeQuery(id+"F28.imprint","IMPRINT",EDGE,{"derivedFrom":sQuery(id+"F28.wireOp",EDGE,"E64.2.22.0")}),-1.0]])]});
            var Q9;
            Q9=makeQuery(id+"F28.imprint","IMPRINT",FACE,{"disambiguationData":[TD([[makeQuery(id+"F28.imprint","IMPRINT",EDGE,{"derivedFrom":sQuery(id+"F28.wireOp",EDGE,"E64.2.23.0")}),-1.0]])]});
            var Q10;
            Q10=makeQuery(id+"F28.imprint","IMPRINT",FACE,{"disambiguationData":[TD([[makeQuery(id+"F28.imprint","IMPRINT",EDGE,{"derivedFrom":sQuery(id+"F28.wireOp",EDGE,"E64.2.24.0")}),-1.0]])]});
            var Q11;
            {var subQ0=sQuery(id+"F28.wireOp",EDGE,"E64.2.25.0");Q11=makeQuery(id+"F28.imprint","IMPRINT",FACE,{"disambiguationData":[TD([[makeQuery(id+"F28.imprint","IMPRINT",EDGE,{"derivedFrom":subQ0}),-1.0]])]});}
            var Q12;
            {var subQ0=sQuery(id+"F28.wireOp",EDGE,"E64.2.26.0");Q12=makeQuery(id+"F28.imprint","IMPRINT",FACE,{"disambiguationData":[TD([[makeQuery(id+"F28.imprint","IMPRINT",EDGE,{"derivedFrom":subQ0}),-1.0]])]});}
            var Q13;
            Q13=makeQuery(id+"F28.imprint","IMPRINT",FACE,{"disambiguationData":[TD([[makeQuery(id+"F28.imprint","IMPRINT",EDGE,{"derivedFrom":sQuery(id+"F28.wireOp",EDGE,"E64.2.27.0")}),-1.0]])]});
            var Q14;
            Q14=makeQuery(id+"F28.imprint","IMPRINT",FACE,{"disambiguationData":[TD([[makeQuery(id+"F28.imprint","IMPRINT",EDGE,{"derivedFrom":sQuery(id+"F28.wireOp",EDGE,"E64.2.28.0")}),-1.0]])]});
            var Q15;
            Q15=makeQuery(id+"F28.imprint","IMPRINT",FACE,{"disambiguationData":[TD([[makeQuery(id+"F28.imprint","IMPRINT",EDGE,{"derivedFrom":sQuery(id+"F28.wireOp",EDGE,"E64.2.29.0")}),-1.0]])]});
            extrude(context, id + "F32", {"entities" : qUnion([Q0, Q1, Q2, Q3, Q4, Q5, Q6, Q7, Q8, Q9, Q10, Q11, Q12, Q13, Q14, Q15]), "operationType" : NewBodyOperationType.ADD, "depth" : 24.9 * mm});
        }
        {
            var Q0;
            {var subQ0=sQuery(id+"F27.wireOp",EDGE,"E41");Q0=makeQuery(id+"F27.imprint","IMPRINT",FACE,{"disambiguationData":[TD([[makeQuery(id+"F27.imprint","IMPRINT",EDGE,{"derivedFrom":subQ0}),1.0]])]});}
            extrude(context, id + "F33", {"entities" : qUnion([Q0]), "operationType" : NewBodyOperationType.ADD, "depth" : 12.2 * mm});
        }
    });
